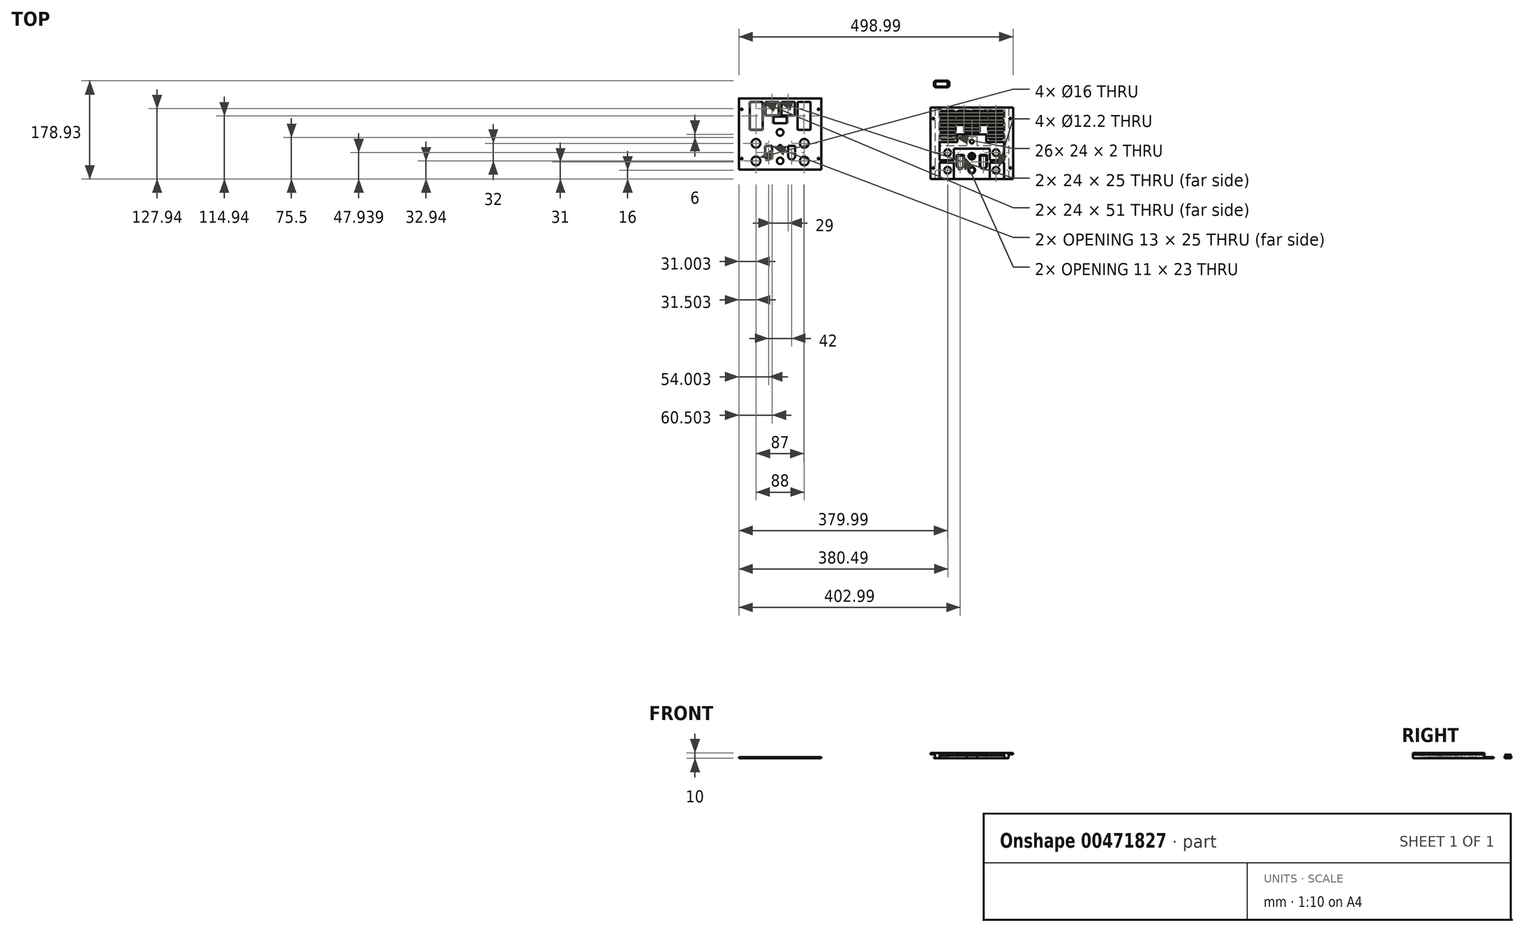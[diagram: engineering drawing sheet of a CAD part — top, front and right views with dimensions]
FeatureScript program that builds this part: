
annotation { "Feature Type Name" : "Feature", "Feature Type Description" : "" }
export const myFeature = defineFeature(function(context is Context, id is Id, definition is map)
    precondition{}
    {
        {
            var Q0;
            Q0=qCreatedBy(makeId("Top.planeOp"),FACE);
            var sketch = newSketch(context, id + "F0", { "sketchPlane" : qUnion([Q0])});
            skLineSegment(sketch, "E0.bottom", {"start": v(75, -65) * mm, "end": v(-75, -65) * mm});
            skLineSegment(sketch, "E0.top", {"start": v(75, 65) * mm, "end": v(-75, 65) * mm});
            skLineSegment(sketch, "E0.left", {"start": v(75, -65) * mm, "end": v(75, 65) * mm});
            skLineSegment(sketch, "E0.right", {"start": v(-75, -65) * mm, "end": v(-75, 65) * mm});
            skPoint(sketch, "E0.middle", {"position": v(0, 0) * mm});
            skLineSegment(sketch, "E1.bottom", {"start": v(-75, 65) * mm, "end": v(-65, 65) * mm, "construction": true});
            skLineSegment(sketch, "E1.top", {"start": v(-75, -65) * mm, "end": v(-65, -65) * mm, "construction": true});
            skLineSegment(sketch, "E1.left", {"start": v(-75, 65) * mm, "end": v(-75, -65) * mm, "construction": true});
            skLineSegment(sketch, "E1.right", {"start": v(-65, 65) * mm, "end": v(-65, -65) * mm, "construction": true});
            skLineSegment(sketch, "E2.bottom", {"start": v(75, -65) * mm, "end": v(65, -65) * mm, "construction": true});
            skLineSegment(sketch, "E2.top", {"start": v(75, 65) * mm, "end": v(65, 65) * mm, "construction": true});
            skLineSegment(sketch, "E2.left", {"start": v(75, -65) * mm, "end": v(75, 65) * mm, "construction": true});
            skLineSegment(sketch, "E2.right", {"start": v(65, -65) * mm, "end": v(65, 65) * mm, "construction": true});
            skCircle(sketch, "E3", {"center": v(-44, -17) * mm, "radius": 6.1 * mm});
            skCircle(sketch, "E4", {"center": v(-44, -49) * mm, "radius": 6.1 * mm});
            skCircle(sketch, "E5", {"center": v(44, -17) * mm, "radius": 6.1 * mm});
            skCircle(sketch, "E6", {"center": v(44, -49) * mm, "radius": 6.1 * mm});
            skCircle(sketch, "E7", {"center": v(0, -49) * mm, "radius": 6 * mm});
            skCircle(sketch, "E8", {"center": v(0, -23.67) * mm, "radius": 6 * mm});
            skLineSegment(sketch, "E9.bottom", {"start": v(-27.5, -21.5) * mm, "end": v(-14.5, -21.5) * mm});
            skLineSegment(sketch, "E9.top", {"start": v(-21, -46.5) * mm, "end": v(-21, -46.5) * mm});
            skLineSegment(sketch, "E9.left", {"start": v(-27.5, -21.5) * mm, "end": v(-27.5, -40) * mm});
            skLineSegment(sketch, "E9.right", {"start": v(-14.5, -21.5) * mm, "end": v(-14.5, -40) * mm});
            skPoint(sketch, "E10.visualSharp", {"position": v(-27.5, -46.5) * mm});
            skArc(sketch, "E10.filletArc", {"start": v(-27.5, -40) * mm, "mid": v(-25.6, -44.6) * mm, "end": v(-21, -46.5) * mm});
            skPoint(sketch, "E11.visualSharp", {"position": v(-14.5, -46.5) * mm});
            skArc(sketch, "E11.filletArc", {"start": v(-21, -46.5) * mm, "mid": v(-16.4, -44.6) * mm, "end": v(-14.5, -40) * mm});
            skLineSegment(sketch, "E12.bottom", {"start": v(14.5, -21.5) * mm, "end": v(27.5, -21.5) * mm});
            skLineSegment(sketch, "E12.top", {"start": v(21, -46.5) * mm, "end": v(21, -46.5) * mm});
            skLineSegment(sketch, "E12.left", {"start": v(14.5, -21.5) * mm, "end": v(14.5, -40) * mm});
            skLineSegment(sketch, "E12.right", {"start": v(27.5, -21.5) * mm, "end": v(27.5, -40) * mm});
            skPoint(sketch, "E13.visualSharp", {"position": v(14.5, -46.5) * mm});
            skArc(sketch, "E13.filletArc", {"start": v(14.5, -40) * mm, "mid": v(16.4, -44.6) * mm, "end": v(21, -46.5) * mm});
            skPoint(sketch, "E14.visualSharp", {"position": v(27.5, -46.5) * mm});
            skArc(sketch, "E14.filletArc", {"start": v(21, -46.5) * mm, "mid": v(25.6, -44.6) * mm, "end": v(27.5, -40) * mm});
            skLineSegment(sketch, "E15.bottom", {"start": v(56.5, 6.5) * mm, "end": v(-56.5, 6.5) * mm});
            skLineSegment(sketch, "E15.top", {"start": v(56.5, 59.5) * mm, "end": v(-56.5, 59.5) * mm, "construction": true});
            skLineSegment(sketch, "E15.left", {"start": v(56.5, 6.5) * mm, "end": v(56.5, 59.5) * mm, "construction": true});
            skLineSegment(sketch, "E15.right", {"start": v(-56.5, 6.5) * mm, "end": v(-56.5, 59.5) * mm, "construction": true});
            skPoint(sketch, "E15.middle", {"position": v(0, 33) * mm});
            skCircle(sketch, "E16", {"center": v(-44, -17) * mm, "radius": 8 * mm, "construction": true});
            skCircle(sketch, "E17", {"center": v(-44, -49) * mm, "radius": 8 * mm, "construction": true});
            skCircle(sketch, "E18", {"center": v(44, -49) * mm, "radius": 8 * mm, "construction": true});
            skCircle(sketch, "E19", {"center": v(44, -17) * mm, "radius": 8 * mm, "construction": true});
            skLineSegment(sketch, "E20.bottom", {"start": v(-31.5, 46.5) * mm, "end": v(-55.5, 46.5) * mm, "construction": true});
            skLineSegment(sketch, "E20.top", {"start": v(-31.5, 58.5) * mm, "end": v(-55.5, 58.5) * mm, "construction": true});
            skLineSegment(sketch, "E20.left", {"start": v(-31.5, 46.5) * mm, "end": v(-31.5, 58.5) * mm, "construction": true});
            skLineSegment(sketch, "E20.right", {"start": v(-55.5, 46.5) * mm, "end": v(-55.5, 58.5) * mm, "construction": true});
            skPoint(sketch, "E20.middle", {"position": v(-43.5, 52.5) * mm});
            skLineSegment(sketch, "E21.bottom", {"start": v(-31.5, 45.5) * mm, "end": v(-55.5, 45.5) * mm, "construction": true});
            skLineSegment(sketch, "E21.top", {"start": v(-31.5, 33.5) * mm, "end": v(-55.5, 33.5) * mm, "construction": true});
            skLineSegment(sketch, "E21.left", {"start": v(-31.5, 45.5) * mm, "end": v(-31.5, 33.5) * mm, "construction": true});
            skLineSegment(sketch, "E21.right", {"start": v(-55.5, 45.5) * mm, "end": v(-55.5, 33.5) * mm, "construction": true});
            skPoint(sketch, "E21.middle", {"position": v(-43.5, 39.5) * mm});
            skLineSegment(sketch, "E22.bottom", {"start": v(-31.5, 32.5) * mm, "end": v(-55.5, 32.5) * mm, "construction": true});
            skLineSegment(sketch, "E22.top", {"start": v(-31.5, 20.5) * mm, "end": v(-55.5, 20.5) * mm, "construction": true});
            skLineSegment(sketch, "E22.left", {"start": v(-31.5, 32.5) * mm, "end": v(-31.5, 20.5) * mm, "construction": true});
            skLineSegment(sketch, "E22.right", {"start": v(-55.5, 32.5) * mm, "end": v(-55.5, 20.5) * mm, "construction": true});
            skPoint(sketch, "E22.middle", {"position": v(-43.5, 26.5) * mm});
            skLineSegment(sketch, "E23.bottom", {"start": v(-31.5, 19.5) * mm, "end": v(-55.5, 19.5) * mm, "construction": true});
            skLineSegment(sketch, "E23.top", {"start": v(-31.5, 7.5) * mm, "end": v(-55.5, 7.5) * mm, "construction": true});
            skLineSegment(sketch, "E23.left", {"start": v(-31.5, 19.5) * mm, "end": v(-31.5, 7.5) * mm, "construction": true});
            skLineSegment(sketch, "E23.right", {"start": v(-55.5, 19.5) * mm, "end": v(-55.5, 7.5) * mm, "construction": true});
            skPoint(sketch, "E23.middle", {"position": v(-43.5, 13.5) * mm});
            skLineSegment(sketch, "E24.bottom", {"start": v(55.5, 32.5) * mm, "end": v(31.5, 32.5) * mm, "construction": true});
            skLineSegment(sketch, "E24.top", {"start": v(55.5, 20.5) * mm, "end": v(31.5, 20.5) * mm, "construction": true});
            skLineSegment(sketch, "E24.left", {"start": v(55.5, 32.5) * mm, "end": v(55.5, 20.5) * mm, "construction": true});
            skLineSegment(sketch, "E24.right", {"start": v(31.5, 32.5) * mm, "end": v(31.5, 20.5) * mm, "construction": true});
            skPoint(sketch, "E24.middle", {"position": v(43.5, 26.5) * mm});
            skLineSegment(sketch, "E25.bottom", {"start": v(55.5, 19.5) * mm, "end": v(31.5, 19.5) * mm, "construction": true});
            skLineSegment(sketch, "E25.top", {"start": v(55.5, 7.5) * mm, "end": v(31.5, 7.5) * mm, "construction": true});
            skLineSegment(sketch, "E25.left", {"start": v(55.5, 19.5) * mm, "end": v(55.5, 7.5) * mm, "construction": true});
            skLineSegment(sketch, "E25.right", {"start": v(31.5, 19.5) * mm, "end": v(31.5, 7.5) * mm, "construction": true});
            skPoint(sketch, "E25.middle", {"position": v(43.5, 13.5) * mm});
            skPoint(sketch, "E25.middle.positionSnap0", {"position": v(43.5, 20.5) * mm});
            skPoint(sketch, "E25.centerSnap0", {"position": v(43.5, 20.5) * mm});
            skLineSegment(sketch, "E26.bottom", {"start": v(12, 20.33) * mm, "end": v(-12, 20.33) * mm, "construction": true});
            skLineSegment(sketch, "E26.top", {"start": v(12, 32.33) * mm, "end": v(-12, 32.33) * mm, "construction": true});
            skLineSegment(sketch, "E26.left", {"start": v(12, 20.33) * mm, "end": v(12, 32.33) * mm, "construction": true});
            skLineSegment(sketch, "E26.right", {"start": v(-12, 20.33) * mm, "end": v(-12, 32.33) * mm, "construction": true});
            skPoint(sketch, "E26.middle", {"position": v(0, 26.33) * mm});
            skCircle(sketch, "E27", {"center": v(-70, 45) * mm, "radius": 1.5 * mm});
            skCircle(sketch, "E28", {"center": v(-70, -45) * mm, "radius": 1.5 * mm});
            skCircle(sketch, "E29", {"center": v(70, 45) * mm, "radius": 1.5 * mm});
            skCircle(sketch, "E30", {"center": v(70, -45) * mm, "radius": 1.5 * mm});
            skCircle(sketch, "E31", {"center": v(0, 3) * mm, "radius": 3.5 * mm});
            skCircle(sketch, "E32", {"center": v(0, 3) * mm, "radius": 6.15 * mm, "construction": true});
            skLineSegment(sketch, "E33.bottom", {"start": v(-30.46, 6.5) * mm, "end": v(-12.96, 6.5) * mm});
            skLineSegment(sketch, "E33.top", {"start": v(-30.46, 32.33) * mm, "end": v(-12.96, 32.33) * mm, "construction": true});
            skLineSegment(sketch, "E33.left", {"start": v(-30.46, 6.5) * mm, "end": v(-30.46, 32.33) * mm, "construction": true});
            skLineSegment(sketch, "E33.right", {"start": v(-12.96, 19.33) * mm, "end": v(-12.96, 32.33) * mm, "construction": true});
            skLineSegment(sketch, "E34.bottom", {"start": v(13.04, 32.33) * mm, "end": v(30.54, 32.33) * mm, "construction": true});
            skLineSegment(sketch, "E34.top", {"start": v(13.04, 6.5) * mm, "end": v(30.54, 6.5) * mm});
            skLineSegment(sketch, "E34.left", {"start": v(13.04, 32.33) * mm, "end": v(13.04, 19.33) * mm, "construction": true});
            skLineSegment(sketch, "E34.right", {"start": v(30.54, 32.33) * mm, "end": v(30.54, 6.5) * mm, "construction": true});
            skLineSegment(sketch, "E35", {"start": v(-12.96, 19.33) * mm, "end": v(13.04, 19.33) * mm, "construction": true});
            skLineSegment(sketch, "E36.bottom", {"start": v(-55.5, 57.5) * mm, "end": v(-57.5, 57.5) * mm, "construction": true});
            skLineSegment(sketch, "E36.top", {"start": v(-55.5, 47.5) * mm, "end": v(-57.5, 47.5) * mm, "construction": true});
            skLineSegment(sketch, "E36.left", {"start": v(-55.5, 57.5) * mm, "end": v(-55.5, 47.5) * mm, "construction": true});
            skLineSegment(sketch, "E36.right", {"start": v(-57.5, 57.5) * mm, "end": v(-57.5, 47.5) * mm, "construction": true});
            skLineSegment(sketch, "E37.bottom", {"start": v(-31.5, 57.5) * mm, "end": v(-29.5, 57.5) * mm, "construction": true});
            skLineSegment(sketch, "E37.top", {"start": v(-31.5, 47.5) * mm, "end": v(-29.5, 47.5) * mm, "construction": true});
            skLineSegment(sketch, "E37.left", {"start": v(-31.5, 57.5) * mm, "end": v(-31.5, 47.5) * mm, "construction": true});
            skLineSegment(sketch, "E37.right", {"start": v(-29.5, 57.5) * mm, "end": v(-29.5, 47.5) * mm, "construction": true});
            skLineSegment(sketch, "E38.bottom", {"start": v(-55.5, 44.5) * mm, "end": v(-57.5, 44.5) * mm, "construction": true});
            skLineSegment(sketch, "E38.top", {"start": v(-55.5, 34.5) * mm, "end": v(-57.5, 34.5) * mm, "construction": true});
            skLineSegment(sketch, "E38.left", {"start": v(-55.5, 44.5) * mm, "end": v(-55.5, 34.5) * mm, "construction": true});
            skLineSegment(sketch, "E38.right", {"start": v(-57.5, 44.5) * mm, "end": v(-57.5, 34.5) * mm, "construction": true});
            skLineSegment(sketch, "E39.bottom", {"start": v(-31.5, 44.5) * mm, "end": v(-29.5, 44.5) * mm, "construction": true});
            skLineSegment(sketch, "E39.top", {"start": v(-31.5, 34.5) * mm, "end": v(-29.5, 34.5) * mm, "construction": true});
            skLineSegment(sketch, "E39.left", {"start": v(-31.5, 44.5) * mm, "end": v(-31.5, 34.5) * mm, "construction": true});
            skLineSegment(sketch, "E39.right", {"start": v(-29.5, 44.5) * mm, "end": v(-29.5, 34.5) * mm, "construction": true});
            skPoint(sketch, "E40.1.0.0", {"position": v(-14.5, 39.5) * mm});
            skLineSegment(sketch, "E40.1.0.1", {"start": v(-2.5, 44.5) * mm, "end": v(-2.5, 34.5) * mm, "construction": true});
            skLineSegment(sketch, "E40.1.0.2", {"start": v(-2.5, 45.5) * mm, "end": v(-26.5, 45.5) * mm, "construction": true});
            skLineSegment(sketch, "E40.1.0.3", {"start": v(-26.5, 44.5) * mm, "end": v(-26.5, 34.5) * mm, "construction": true});
            skLineSegment(sketch, "E40.1.0.4", {"start": v(-2.5, 58.5) * mm, "end": v(-26.5, 58.5) * mm, "construction": true});
            skLineSegment(sketch, "E40.1.0.5", {"start": v(-0.5, 44.5) * mm, "end": v(-0.5, 34.5) * mm, "construction": true});
            skLineSegment(sketch, "E40.1.0.6", {"start": v(-2.5, 47.5) * mm, "end": v(-0.5, 47.5) * mm, "construction": true});
            skLineSegment(sketch, "E40.1.0.7", {"start": v(-26.5, 57.5) * mm, "end": v(-26.5, 47.5) * mm, "construction": true});
            skLineSegment(sketch, "E40.1.0.8", {"start": v(-2.5, 46.5) * mm, "end": v(-26.5, 46.5) * mm, "construction": true});
            skLineSegment(sketch, "E40.1.0.9", {"start": v(-2.5, 33.5) * mm, "end": v(-26.5, 33.5) * mm, "construction": true});
            skLineSegment(sketch, "E40.1.0.10", {"start": v(-28.5, 44.5) * mm, "end": v(-28.5, 34.5) * mm, "construction": true});
            skLineSegment(sketch, "E40.1.0.11", {"start": v(-26.5, 47.5) * mm, "end": v(-28.5, 47.5) * mm, "construction": true});
            skLineSegment(sketch, "E40.1.0.12", {"start": v(-28.5, 57.5) * mm, "end": v(-28.5, 47.5) * mm, "construction": true});
            skLineSegment(sketch, "E40.1.0.13", {"start": v(-26.5, 34.5) * mm, "end": v(-28.5, 34.5) * mm, "construction": true});
            skLineSegment(sketch, "E40.1.0.14", {"start": v(-0.5, 57.5) * mm, "end": v(-0.5, 47.5) * mm, "construction": true});
            skLineSegment(sketch, "E40.1.0.15", {"start": v(-2.5, 46.5) * mm, "end": v(-2.5, 58.5) * mm, "construction": true});
            skLineSegment(sketch, "E40.1.0.16", {"start": v(-2.5, 44.5) * mm, "end": v(-0.5, 44.5) * mm, "construction": true});
            skLineSegment(sketch, "E40.1.0.17", {"start": v(-2.5, 57.5) * mm, "end": v(-0.5, 57.5) * mm, "construction": true});
            skLineSegment(sketch, "E40.1.0.18", {"start": v(-2.5, 34.5) * mm, "end": v(-0.5, 34.5) * mm, "construction": true});
            skLineSegment(sketch, "E40.1.0.19", {"start": v(-26.5, 57.5) * mm, "end": v(-28.5, 57.5) * mm, "construction": true});
            skPoint(sketch, "E40.1.0.20", {"position": v(-14.5, 52.5) * mm});
            skLineSegment(sketch, "E40.1.0.21", {"start": v(-26.5, 44.5) * mm, "end": v(-28.5, 44.5) * mm, "construction": true});
            skLineSegment(sketch, "E40.1.0.22", {"start": v(-2.5, 57.5) * mm, "end": v(-2.5, 47.5) * mm, "construction": true});
            skLineSegment(sketch, "E40.1.0.23", {"start": v(-26.5, 46.5) * mm, "end": v(-26.5, 58.5) * mm, "construction": true});
            skLineSegment(sketch, "E40.1.0.24", {"start": v(-26.5, 45.5) * mm, "end": v(-26.5, 33.5) * mm, "construction": true});
            skLineSegment(sketch, "E40.1.0.25", {"start": v(-2.5, 45.5) * mm, "end": v(-2.5, 33.5) * mm, "construction": true});
            skPoint(sketch, "E40.2.0.0", {"position": v(14.5, 39.5) * mm});
            skLineSegment(sketch, "E40.2.0.1", {"start": v(26.5, 44.5) * mm, "end": v(26.5, 34.5) * mm, "construction": true});
            skLineSegment(sketch, "E40.2.0.2", {"start": v(26.5, 45.5) * mm, "end": v(2.5, 45.5) * mm, "construction": true});
            skLineSegment(sketch, "E40.2.0.3", {"start": v(2.5, 44.5) * mm, "end": v(2.5, 34.5) * mm, "construction": true});
            skLineSegment(sketch, "E40.2.0.4", {"start": v(26.5, 58.5) * mm, "end": v(2.5, 58.5) * mm, "construction": true});
            skLineSegment(sketch, "E40.2.0.5", {"start": v(28.5, 44.5) * mm, "end": v(28.5, 34.5) * mm, "construction": true});
            skLineSegment(sketch, "E40.2.0.6", {"start": v(26.5, 47.5) * mm, "end": v(28.5, 47.5) * mm, "construction": true});
            skLineSegment(sketch, "E40.2.0.7", {"start": v(2.5, 57.5) * mm, "end": v(2.5, 47.5) * mm, "construction": true});
            skLineSegment(sketch, "E40.2.0.8", {"start": v(26.5, 46.5) * mm, "end": v(2.5, 46.5) * mm, "construction": true});
            skLineSegment(sketch, "E40.2.0.9", {"start": v(26.5, 33.5) * mm, "end": v(2.5, 33.5) * mm, "construction": true});
            skLineSegment(sketch, "E40.2.0.10", {"start": v(0.5, 44.5) * mm, "end": v(0.5, 34.5) * mm, "construction": true});
            skLineSegment(sketch, "E40.2.0.11", {"start": v(2.5, 47.5) * mm, "end": v(0.5, 47.5) * mm, "construction": true});
            skLineSegment(sketch, "E40.2.0.12", {"start": v(0.5, 57.5) * mm, "end": v(0.5, 47.5) * mm, "construction": true});
            skLineSegment(sketch, "E40.2.0.13", {"start": v(2.5, 34.5) * mm, "end": v(0.5, 34.5) * mm, "construction": true});
            skLineSegment(sketch, "E40.2.0.14", {"start": v(28.5, 57.5) * mm, "end": v(28.5, 47.5) * mm, "construction": true});
            skLineSegment(sketch, "E40.2.0.15", {"start": v(26.5, 46.5) * mm, "end": v(26.5, 58.5) * mm, "construction": true});
            skLineSegment(sketch, "E40.2.0.16", {"start": v(26.5, 44.5) * mm, "end": v(28.5, 44.5) * mm, "construction": true});
            skLineSegment(sketch, "E40.2.0.17", {"start": v(26.5, 57.5) * mm, "end": v(28.5, 57.5) * mm, "construction": true});
            skLineSegment(sketch, "E40.2.0.18", {"start": v(26.5, 34.5) * mm, "end": v(28.5, 34.5) * mm, "construction": true});
            skLineSegment(sketch, "E40.2.0.19", {"start": v(2.5, 57.5) * mm, "end": v(0.5, 57.5) * mm, "construction": true});
            skPoint(sketch, "E40.2.0.20", {"position": v(14.5, 52.5) * mm});
            skLineSegment(sketch, "E40.2.0.21", {"start": v(2.5, 44.5) * mm, "end": v(0.5, 44.5) * mm, "construction": true});
            skLineSegment(sketch, "E40.2.0.22", {"start": v(26.5, 57.5) * mm, "end": v(26.5, 47.5) * mm, "construction": true});
            skLineSegment(sketch, "E40.2.0.23", {"start": v(2.5, 46.5) * mm, "end": v(2.5, 58.5) * mm, "construction": true});
            skLineSegment(sketch, "E40.2.0.24", {"start": v(2.5, 45.5) * mm, "end": v(2.5, 33.5) * mm, "construction": true});
            skLineSegment(sketch, "E40.2.0.25", {"start": v(26.5, 45.5) * mm, "end": v(26.5, 33.5) * mm, "construction": true});
            skPoint(sketch, "E40.3.0.0", {"position": v(43.5, 39.5) * mm});
            skLineSegment(sketch, "E40.3.0.1", {"start": v(55.5, 44.5) * mm, "end": v(55.5, 34.5) * mm, "construction": true});
            skLineSegment(sketch, "E40.3.0.2", {"start": v(55.5, 45.5) * mm, "end": v(31.5, 45.5) * mm, "construction": true});
            skLineSegment(sketch, "E40.3.0.3", {"start": v(31.5, 44.5) * mm, "end": v(31.5, 34.5) * mm, "construction": true});
            skLineSegment(sketch, "E40.3.0.4", {"start": v(55.5, 58.5) * mm, "end": v(31.5, 58.5) * mm, "construction": true});
            skLineSegment(sketch, "E40.3.0.5", {"start": v(57.5, 44.5) * mm, "end": v(57.5, 34.5) * mm, "construction": true});
            skLineSegment(sketch, "E40.3.0.6", {"start": v(55.5, 47.5) * mm, "end": v(57.5, 47.5) * mm, "construction": true});
            skLineSegment(sketch, "E40.3.0.7", {"start": v(31.5, 57.5) * mm, "end": v(31.5, 47.5) * mm, "construction": true});
            skLineSegment(sketch, "E40.3.0.8", {"start": v(55.5, 46.5) * mm, "end": v(31.5, 46.5) * mm, "construction": true});
            skLineSegment(sketch, "E40.3.0.9", {"start": v(55.5, 33.5) * mm, "end": v(31.5, 33.5) * mm, "construction": true});
            skLineSegment(sketch, "E40.3.0.10", {"start": v(29.5, 44.5) * mm, "end": v(29.5, 34.5) * mm, "construction": true});
            skLineSegment(sketch, "E40.3.0.11", {"start": v(31.5, 47.5) * mm, "end": v(29.5, 47.5) * mm, "construction": true});
            skLineSegment(sketch, "E40.3.0.12", {"start": v(29.5, 57.5) * mm, "end": v(29.5, 47.5) * mm, "construction": true});
            skLineSegment(sketch, "E40.3.0.13", {"start": v(31.5, 34.5) * mm, "end": v(29.5, 34.5) * mm, "construction": true});
            skLineSegment(sketch, "E40.3.0.14", {"start": v(57.5, 57.5) * mm, "end": v(57.5, 47.5) * mm, "construction": true});
            skLineSegment(sketch, "E40.3.0.15", {"start": v(55.5, 46.5) * mm, "end": v(55.5, 58.5) * mm, "construction": true});
            skLineSegment(sketch, "E40.3.0.16", {"start": v(55.5, 44.5) * mm, "end": v(57.5, 44.5) * mm, "construction": true});
            skLineSegment(sketch, "E40.3.0.17", {"start": v(55.5, 57.5) * mm, "end": v(57.5, 57.5) * mm, "construction": true});
            skLineSegment(sketch, "E40.3.0.18", {"start": v(55.5, 34.5) * mm, "end": v(57.5, 34.5) * mm, "construction": true});
            skLineSegment(sketch, "E40.3.0.19", {"start": v(31.5, 57.5) * mm, "end": v(29.5, 57.5) * mm, "construction": true});
            skPoint(sketch, "E40.3.0.20", {"position": v(43.5, 52.5) * mm});
            skLineSegment(sketch, "E40.3.0.21", {"start": v(31.5, 44.5) * mm, "end": v(29.5, 44.5) * mm, "construction": true});
            skLineSegment(sketch, "E40.3.0.22", {"start": v(55.5, 57.5) * mm, "end": v(55.5, 47.5) * mm, "construction": true});
            skLineSegment(sketch, "E40.3.0.23", {"start": v(31.5, 46.5) * mm, "end": v(31.5, 58.5) * mm, "construction": true});
            skLineSegment(sketch, "E40.3.0.24", {"start": v(31.5, 45.5) * mm, "end": v(31.5, 33.5) * mm, "construction": true});
            skLineSegment(sketch, "E40.3.0.25", {"start": v(55.5, 45.5) * mm, "end": v(55.5, 33.5) * mm, "construction": true});
            skLineSegment(sketch, "E40.direction1", {"start": v(-57.5, 34.5) * mm, "end": v(-28.5, 34.5) * mm, "construction": true});
            skSolve(sketch);
        }
        {
            var Q0;
            Q0=makeQuery(id+"F0.imprint","IMPRINT",FACE,{"disambiguationData":[TD([[makeQuery(id+"F0.imprint","IMPRINT",EDGE,{"derivedFrom":sQuery(id+"F0.wireOp",EDGE,"E0.bottom")}),-1.0]])]});
            var Q1;
            {var subQ3=sQuery(id+"F0.wireOp",EDGE,"E33.bottom");Q1=makeQuery(id+"F0.imprint","IMPRINT",FACE,{"disambiguationData":[TD([[makeQuery(id+"F0.imprint","IMPRINT",EDGE,{"derivedFrom":subQ3}),1.0]])]});}
            extrude(context, id + "F1", {"entities" : qUnion([Q0, Q1]), "depth" : 10 * mm});
        }
        {
            var Q0;
            Q0=qCreatedBy(makeId("Top.planeOp"),FACE);
            var sketch = newSketch(context, id + "F2", { "sketchPlane" : qUnion([Q0])});
            skLineSegment(sketch, "E41.bottom", {"start": v(-273.99, -48.06) * mm, "end": v(-423.99, -48.06) * mm});
            skLineSegment(sketch, "E41.top", {"start": v(-273.99, 81.94) * mm, "end": v(-423.99, 81.94) * mm});
            skLineSegment(sketch, "E41.left", {"start": v(-273.99, -48.06) * mm, "end": v(-273.99, 81.94) * mm});
            skLineSegment(sketch, "E41.right", {"start": v(-423.99, -48.06) * mm, "end": v(-423.99, 81.94) * mm});
            skPoint(sketch, "E41.middle", {"position": v(-348.99, 16.94) * mm});
            skLineSegment(sketch, "E42.bottom", {"start": v(-423.99, 81.94) * mm, "end": v(-413.99, 81.94) * mm, "construction": true});
            skLineSegment(sketch, "E42.top", {"start": v(-423.99, -48.06) * mm, "end": v(-413.99, -48.06) * mm, "construction": true});
            skLineSegment(sketch, "E42.left", {"start": v(-423.99, 81.94) * mm, "end": v(-423.99, -48.06) * mm, "construction": true});
            skLineSegment(sketch, "E42.right", {"start": v(-413.99, 81.94) * mm, "end": v(-413.99, -48.06) * mm, "construction": true});
            skLineSegment(sketch, "E43.bottom", {"start": v(-273.99, -48.06) * mm, "end": v(-283.99, -48.06) * mm, "construction": true});
            skLineSegment(sketch, "E43.top", {"start": v(-273.99, 81.94) * mm, "end": v(-283.99, 81.94) * mm, "construction": true});
            skLineSegment(sketch, "E43.left", {"start": v(-273.99, -48.06) * mm, "end": v(-273.99, 81.94) * mm, "construction": true});
            skLineSegment(sketch, "E43.right", {"start": v(-283.99, -48.06) * mm, "end": v(-283.99, 81.94) * mm, "construction": true});
            skCircle(sketch, "E44", {"center": v(-392.99, -0.06) * mm, "radius": 6.1 * mm, "construction": true});
            skCircle(sketch, "E45", {"center": v(-392.99, -32.06) * mm, "radius": 6.1 * mm, "construction": true});
            skCircle(sketch, "E46", {"center": v(-304.99, -0.06) * mm, "radius": 6.1 * mm, "construction": true});
            skCircle(sketch, "E47", {"center": v(-304.99, -32.06) * mm, "radius": 6.1 * mm, "construction": true});
            skCircle(sketch, "E48", {"center": v(-348.99, -32.06) * mm, "radius": 6 * mm});
            skCircle(sketch, "E49", {"center": v(-348.99, -6.73) * mm, "radius": 3.5 * mm});
            skLineSegment(sketch, "E50.bottom", {"start": v(-376.49, -4.56) * mm, "end": v(-363.49, -4.56) * mm});
            skLineSegment(sketch, "E50.top", {"start": v(-369.99, -29.56) * mm, "end": v(-369.99, -29.56) * mm});
            skLineSegment(sketch, "E50.left", {"start": v(-376.49, -4.56) * mm, "end": v(-376.49, -23.06) * mm});
            skLineSegment(sketch, "E50.right", {"start": v(-363.49, -4.56) * mm, "end": v(-363.49, -23.06) * mm});
            skPoint(sketch, "E51.visualSharp", {"position": v(-376.49, -29.56) * mm});
            skArc(sketch, "E51.filletArc", {"start": v(-376.49, -23.06) * mm, "mid": v(-374.58, -27.66) * mm, "end": v(-369.99, -29.56) * mm});
            skPoint(sketch, "E52.visualSharp", {"position": v(-363.49, -29.56) * mm});
            skArc(sketch, "E52.filletArc", {"start": v(-369.99, -29.56) * mm, "mid": v(-365.4, -27.66) * mm, "end": v(-363.49, -23.06) * mm});
            skLineSegment(sketch, "E53.bottom", {"start": v(-334.49, -4.56) * mm, "end": v(-321.49, -4.56) * mm});
            skLineSegment(sketch, "E53.top", {"start": v(-327.99, -29.56) * mm, "end": v(-327.99, -29.56) * mm});
            skLineSegment(sketch, "E53.left", {"start": v(-334.49, -4.56) * mm, "end": v(-334.49, -23.06) * mm});
            skLineSegment(sketch, "E53.right", {"start": v(-321.49, -4.56) * mm, "end": v(-321.49, -23.06) * mm});
            skPoint(sketch, "E54.visualSharp", {"position": v(-334.49, -29.56) * mm});
            skArc(sketch, "E54.filletArc", {"start": v(-334.49, -23.06) * mm, "mid": v(-332.58, -27.66) * mm, "end": v(-327.99, -29.56) * mm});
            skPoint(sketch, "E55.visualSharp", {"position": v(-321.49, -29.56) * mm});
            skArc(sketch, "E55.filletArc", {"start": v(-327.99, -29.56) * mm, "mid": v(-323.4, -27.66) * mm, "end": v(-321.49, -23.06) * mm});
            skPoint(sketch, "E56.middle", {"position": v(-348.99, 49.94) * mm});
            skCircle(sketch, "E57", {"center": v(-392.99, -0.06) * mm, "radius": 8 * mm});
            skCircle(sketch, "E58", {"center": v(-392.99, -32.06) * mm, "radius": 8 * mm});
            skCircle(sketch, "E59", {"center": v(-304.99, -32.06) * mm, "radius": 8 * mm});
            skCircle(sketch, "E60", {"center": v(-304.99, -0.06) * mm, "radius": 8 * mm});
            skLineSegment(sketch, "E61.bottom", {"start": v(-380.49, 63.44) * mm, "end": v(-404.49, 63.44) * mm, "construction": true});
            skLineSegment(sketch, "E61.top", {"start": v(-380.49, 75.44) * mm, "end": v(-404.49, 75.44) * mm, "construction": true});
            skLineSegment(sketch, "E61.left", {"start": v(-380.49, 63.44) * mm, "end": v(-380.49, 75.44) * mm, "construction": true});
            skLineSegment(sketch, "E61.right", {"start": v(-404.49, 63.44) * mm, "end": v(-404.49, 75.44) * mm, "construction": true});
            skPoint(sketch, "E61.middle", {"position": v(-392.49, 69.44) * mm});
            skLineSegment(sketch, "E62.bottom", {"start": v(-380.49, 62.44) * mm, "end": v(-404.49, 62.44) * mm, "construction": true});
            skLineSegment(sketch, "E62.top", {"start": v(-380.49, 50.44) * mm, "end": v(-404.49, 50.44) * mm, "construction": true});
            skLineSegment(sketch, "E62.left", {"start": v(-380.49, 62.44) * mm, "end": v(-380.49, 50.44) * mm, "construction": true});
            skLineSegment(sketch, "E62.right", {"start": v(-404.49, 62.44) * mm, "end": v(-404.49, 50.44) * mm, "construction": true});
            skPoint(sketch, "E62.middle", {"position": v(-392.49, 56.44) * mm});
            skLineSegment(sketch, "E63.bottom", {"start": v(-380.49, 49.44) * mm, "end": v(-404.49, 49.44) * mm, "construction": true});
            skLineSegment(sketch, "E63.top", {"start": v(-380.49, 37.44) * mm, "end": v(-404.49, 37.44) * mm, "construction": true});
            skLineSegment(sketch, "E63.left", {"start": v(-380.49, 49.44) * mm, "end": v(-380.49, 37.44) * mm, "construction": true});
            skLineSegment(sketch, "E63.right", {"start": v(-404.49, 49.44) * mm, "end": v(-404.49, 37.44) * mm, "construction": true});
            skPoint(sketch, "E63.middle", {"position": v(-392.49, 43.44) * mm});
            skLineSegment(sketch, "E64.bottom", {"start": v(-380.49, 36.44) * mm, "end": v(-404.49, 36.44) * mm, "construction": true});
            skLineSegment(sketch, "E64.top", {"start": v(-380.49, 24.44) * mm, "end": v(-404.49, 24.44) * mm, "construction": true});
            skLineSegment(sketch, "E64.left", {"start": v(-380.49, 36.44) * mm, "end": v(-380.49, 24.44) * mm, "construction": true});
            skLineSegment(sketch, "E64.right", {"start": v(-404.49, 36.44) * mm, "end": v(-404.49, 24.44) * mm, "construction": true});
            skPoint(sketch, "E64.middle", {"position": v(-392.49, 30.44) * mm});
            skPoint(sketch, "E65.1.0.0", {"position": v(-363.49, 56.44) * mm});
            skLineSegment(sketch, "E65.1.0.1", {"start": v(-351.49, 62.44) * mm, "end": v(-351.49, 50.44) * mm, "construction": true});
            skLineSegment(sketch, "E65.1.0.2", {"start": v(-351.49, 62.44) * mm, "end": v(-375.49, 62.44) * mm, "construction": true});
            skLineSegment(sketch, "E65.1.0.3", {"start": v(-375.49, 63.44) * mm, "end": v(-375.49, 75.44) * mm, "construction": true});
            skLineSegment(sketch, "E65.1.0.4", {"start": v(-351.49, 75.44) * mm, "end": v(-375.49, 75.44) * mm, "construction": true});
            skPoint(sketch, "E65.1.0.5", {"position": v(-363.49, 69.44) * mm});
            skLineSegment(sketch, "E65.1.0.6", {"start": v(-351.49, 50.44) * mm, "end": v(-375.49, 50.44) * mm, "construction": true});
            skLineSegment(sketch, "E65.1.0.7", {"start": v(-351.49, 63.44) * mm, "end": v(-351.49, 75.44) * mm, "construction": true});
            skLineSegment(sketch, "E65.1.0.8", {"start": v(-375.49, 62.44) * mm, "end": v(-375.49, 50.44) * mm, "construction": true});
            skLineSegment(sketch, "E65.1.0.9", {"start": v(-351.49, 63.44) * mm, "end": v(-375.49, 63.44) * mm, "construction": true});
            skPoint(sketch, "E65.2.0.0", {"position": v(-334.49, 56.44) * mm});
            skLineSegment(sketch, "E65.2.0.1", {"start": v(-322.49, 62.44) * mm, "end": v(-322.49, 50.44) * mm, "construction": true});
            skLineSegment(sketch, "E65.2.0.2", {"start": v(-322.49, 62.44) * mm, "end": v(-346.49, 62.44) * mm, "construction": true});
            skLineSegment(sketch, "E65.2.0.3", {"start": v(-346.49, 63.44) * mm, "end": v(-346.49, 75.44) * mm, "construction": true});
            skLineSegment(sketch, "E65.2.0.4", {"start": v(-322.49, 75.44) * mm, "end": v(-346.49, 75.44) * mm, "construction": true});
            skPoint(sketch, "E65.2.0.5", {"position": v(-334.49, 69.44) * mm});
            skLineSegment(sketch, "E65.2.0.6", {"start": v(-322.49, 50.44) * mm, "end": v(-346.49, 50.44) * mm, "construction": true});
            skLineSegment(sketch, "E65.2.0.7", {"start": v(-322.49, 63.44) * mm, "end": v(-322.49, 75.44) * mm, "construction": true});
            skLineSegment(sketch, "E65.2.0.8", {"start": v(-346.49, 62.44) * mm, "end": v(-346.49, 50.44) * mm, "construction": true});
            skLineSegment(sketch, "E65.2.0.9", {"start": v(-322.49, 63.44) * mm, "end": v(-346.49, 63.44) * mm, "construction": true});
            skPoint(sketch, "E65.3.0.0", {"position": v(-305.49, 56.44) * mm});
            skLineSegment(sketch, "E65.3.0.1", {"start": v(-293.49, 62.44) * mm, "end": v(-293.49, 50.44) * mm, "construction": true});
            skLineSegment(sketch, "E65.3.0.2", {"start": v(-293.49, 62.44) * mm, "end": v(-317.49, 62.44) * mm, "construction": true});
            skLineSegment(sketch, "E65.3.0.3", {"start": v(-317.49, 63.44) * mm, "end": v(-317.49, 75.44) * mm, "construction": true});
            skLineSegment(sketch, "E65.3.0.4", {"start": v(-293.49, 75.44) * mm, "end": v(-317.49, 75.44) * mm, "construction": true});
            skPoint(sketch, "E65.3.0.5", {"position": v(-305.49, 69.44) * mm});
            skLineSegment(sketch, "E65.3.0.6", {"start": v(-293.49, 50.44) * mm, "end": v(-317.49, 50.44) * mm, "construction": true});
            skLineSegment(sketch, "E65.3.0.7", {"start": v(-293.49, 63.44) * mm, "end": v(-293.49, 75.44) * mm, "construction": true});
            skLineSegment(sketch, "E65.3.0.8", {"start": v(-317.49, 62.44) * mm, "end": v(-317.49, 50.44) * mm, "construction": true});
            skLineSegment(sketch, "E65.3.0.9", {"start": v(-293.49, 63.44) * mm, "end": v(-317.49, 63.44) * mm, "construction": true});
            skLineSegment(sketch, "E65.direction1", {"start": v(-404.49, 50.44) * mm, "end": v(-375.49, 50.44) * mm, "construction": true});
            skLineSegment(sketch, "E66.bottom", {"start": v(-293.49, 49.44) * mm, "end": v(-317.49, 49.44) * mm, "construction": true});
            skLineSegment(sketch, "E66.top", {"start": v(-293.49, 37.44) * mm, "end": v(-317.49, 37.44) * mm, "construction": true});
            skLineSegment(sketch, "E66.left", {"start": v(-293.49, 49.44) * mm, "end": v(-293.49, 37.44) * mm, "construction": true});
            skLineSegment(sketch, "E66.right", {"start": v(-317.49, 49.44) * mm, "end": v(-317.49, 37.44) * mm, "construction": true});
            skPoint(sketch, "E66.middle", {"position": v(-305.49, 43.44) * mm});
            skLineSegment(sketch, "E67.bottom", {"start": v(-293.49, 36.44) * mm, "end": v(-317.49, 36.44) * mm, "construction": true});
            skLineSegment(sketch, "E67.top", {"start": v(-293.49, 24.44) * mm, "end": v(-317.49, 24.44) * mm, "construction": true});
            skLineSegment(sketch, "E67.left", {"start": v(-293.49, 36.44) * mm, "end": v(-293.49, 24.44) * mm, "construction": true});
            skLineSegment(sketch, "E67.right", {"start": v(-317.49, 36.44) * mm, "end": v(-317.49, 24.44) * mm, "construction": true});
            skPoint(sketch, "E67.middle", {"position": v(-305.49, 30.44) * mm});
            skPoint(sketch, "E67.middle.positionSnap0", {"position": v(-305.49, 37.44) * mm});
            skPoint(sketch, "E67.centerSnap0", {"position": v(-305.49, 37.44) * mm});
            skLineSegment(sketch, "E68.bottom", {"start": v(-336.99, 36.44) * mm, "end": v(-360.99, 36.44) * mm, "construction": true});
            skLineSegment(sketch, "E68.top", {"start": v(-336.99, 48.44) * mm, "end": v(-360.99, 48.44) * mm, "construction": true});
            skLineSegment(sketch, "E68.left", {"start": v(-336.99, 36.44) * mm, "end": v(-336.99, 48.44) * mm, "construction": true});
            skLineSegment(sketch, "E68.right", {"start": v(-360.99, 36.44) * mm, "end": v(-360.99, 48.44) * mm, "construction": true});
            skPoint(sketch, "E68.middle", {"position": v(-348.99, 42.44) * mm});
            skCircle(sketch, "E69", {"center": v(-418.99, 61.94) * mm, "radius": 1.5 * mm});
            skCircle(sketch, "E70", {"center": v(-418.99, -28.06) * mm, "radius": 1.5 * mm});
            skCircle(sketch, "E71", {"center": v(-278.99, 61.94) * mm, "radius": 1.5 * mm});
            skCircle(sketch, "E72", {"center": v(-278.99, -28.06) * mm, "radius": 1.5 * mm});
            skCircle(sketch, "E73", {"center": v(-348.99, 19.94) * mm, "radius": 3.5 * mm, "construction": true});
            skCircle(sketch, "E74", {"center": v(-348.99, 19.94) * mm, "radius": 6.15 * mm});
            skLineSegment(sketch, "E75", {"start": v(-404.49, 75.44) * mm, "end": v(-404.49, 24.44) * mm});
            skLineSegment(sketch, "E76", {"start": v(-404.49, 24.44) * mm, "end": v(-380.49, 24.44) * mm});
            skLineSegment(sketch, "E77", {"start": v(-380.49, 24.44) * mm, "end": v(-380.49, 50.44) * mm});
            skLineSegment(sketch, "E78", {"start": v(-380.49, 50.44) * mm, "end": v(-360.99, 50.44) * mm});
            skLineSegment(sketch, "E79", {"start": v(-360.99, 50.44) * mm, "end": v(-360.99, 36.44) * mm});
            skLineSegment(sketch, "E80", {"start": v(-360.99, 36.44) * mm, "end": v(-336.99, 36.44) * mm});
            skLineSegment(sketch, "E81", {"start": v(-336.99, 36.44) * mm, "end": v(-336.99, 50.44) * mm});
            skLineSegment(sketch, "E82", {"start": v(-336.99, 50.44) * mm, "end": v(-317.49, 50.44) * mm});
            skLineSegment(sketch, "E83", {"start": v(-317.49, 50.44) * mm, "end": v(-317.49, 24.44) * mm});
            skLineSegment(sketch, "E84", {"start": v(-317.49, 24.44) * mm, "end": v(-293.49, 24.44) * mm});
            skLineSegment(sketch, "E85", {"start": v(-293.49, 24.44) * mm, "end": v(-293.49, 75.44) * mm});
            skLineSegment(sketch, "E86", {"start": v(-293.49, 75.44) * mm, "end": v(-404.49, 75.44) * mm});
            skLineSegment(sketch, "E87", {"start": v(-380.49, 50.44) * mm, "end": v(-380.49, 75.44) * mm});
            skLineSegment(sketch, "E88", {"start": v(-375.49, 75.44) * mm, "end": v(-375.49, 50.44) * mm});
            skLineSegment(sketch, "E89", {"start": v(-322.49, 50.44) * mm, "end": v(-322.49, 75.44) * mm});
            skLineSegment(sketch, "E90", {"start": v(-317.49, 75.44) * mm, "end": v(-317.49, 50.44) * mm});
            skLineSegment(sketch, "E91", {"start": v(-360.99, 50.44) * mm, "end": v(-351.49, 50.44) * mm});
            skLineSegment(sketch, "E92", {"start": v(-351.49, 75.44) * mm, "end": v(-351.49, 50.44) * mm});
            skLineSegment(sketch, "E93", {"start": v(-346.49, 50.44) * mm, "end": v(-346.49, 75.44) * mm});
            skLineSegment(sketch, "E94", {"start": v(-336.99, 50.44) * mm, "end": v(-346.49, 50.44) * mm});
            skLineSegment(sketch, "E95", {"start": v(-360.99, 48.44) * mm, "end": v(-336.99, 48.44) * mm});
            skSolve(sketch);
        }
        {
            var Q0;
            Q0=makeQuery(id+"F2.imprint","IMPRINT",FACE,{"disambiguationData":[TD([[makeQuery(id+"F2.imprint","IMPRINT",EDGE,{"derivedFrom":sQuery(id+"F2.wireOp",EDGE,"E41.bottom")}),-1.0]])]});
            var Q1;
            {var subQ3=sQuery(id+"F2.wireOp",EDGE,"1b6c74bc-5b00-42bc-9f1d-b8e6521042cd.bottom");Q1=makeQuery(id+"F2.imprint","IMPRINT",FACE,{"disambiguationData":[TD([[makeQuery(id+"F2.imprint","IMPRINT",EDGE,{"derivedFrom":subQ3}),1.0]])]});}
            var Q2;
            {var subQ0=sQuery(id+"F2.wireOp",EDGE,"E87");Q2=makeQuery(id+"F2.imprint","IMPRINT",FACE,{"disambiguationData":[TD([[makeQuery(id+"F2.imprint","IMPRINT",EDGE,{"derivedFrom":subQ0}),-1.0]])]});}
            var Q3;
            {var subQ0=sQuery(id+"F2.wireOp",EDGE,"E91");Q3=makeQuery(id+"F2.imprint","IMPRINT",FACE,{"disambiguationData":[TD([[makeQuery(id+"F2.imprint","IMPRINT",EDGE,{"derivedFrom":subQ0}),-1.0]])]});}
            var Q4;
            {var subQ2=sQuery(id+"F2.wireOp",EDGE,"E89");Q4=makeQuery(id+"F2.imprint","IMPRINT",FACE,{"disambiguationData":[TD([[makeQuery(id+"F2.imprint","IMPRINT",EDGE,{"derivedFrom":subQ2}),-1.0]])]});}
            extrude(context, id + "F3", {"entities" : qUnion([Q0, Q1, Q2, Q3, Q4]), "depth" : 2 * mm});
        }
        {
            var Q0;
            Q0=makeQuery(id+"F1.opExtrude","SWEPT_FACE",FACE,{"disambiguationData":[OSD([sQuery(id+"F0.wireOp",EDGE,"E0.bottom")])]});
            var sketch = newSketch(context, id + "F4", { "sketchPlane" : qUnion([Q0])});
            skLineSegment(sketch, "E96.bottom", {"start": v(-75, 0) * mm, "end": v(-67, 0) * mm});
            skLineSegment(sketch, "E96.top", {"start": v(-75, 7) * mm, "end": v(-67, 7) * mm});
            skLineSegment(sketch, "E96.left", {"start": v(-75, 0) * mm, "end": v(-75, 7) * mm});
            skLineSegment(sketch, "E96.right", {"start": v(-67, 0) * mm, "end": v(-67, 7) * mm});
            skLineSegment(sketch, "E97.bottom", {"start": v(75, 0) * mm, "end": v(67, 0) * mm});
            skLineSegment(sketch, "E97.top", {"start": v(75, 7) * mm, "end": v(67, 7) * mm});
            skLineSegment(sketch, "E97.left", {"start": v(75, 0) * mm, "end": v(75, 7) * mm});
            skLineSegment(sketch, "E97.right", {"start": v(67, 0) * mm, "end": v(67, 7) * mm});
            skSolve(sketch);
        }
        {
            var Q0;
            Q0 = qSketchRegion(id + "F4", true);
            extrude(context, id + "F5", {"entities" : qUnion([Q0]), "operationType" : NewBodyOperationType.REMOVE, "oppositeDirection" : true, "depth" : 137.4 * mm});
        }
        {
            var Q0;
            Q0=makeQuery(id+"F1.opExtrude","CAP_FACE",FACE,{"disambiguationData":[OSD([sQuery(id+"F0.wireOp",EDGE,"E0.bottom"),sQuery(id+"F0.wireOp",EDGE,"E0.top"),sQuery(id+"F0.wireOp",EDGE,"E0.left"),sQuery(id+"F0.wireOp",EDGE,"E0.right"),sQuery(id+"F0.wireOp",EDGE,"E3"),sQuery(id+"F0.wireOp",EDGE,"E4"),sQuery(id+"F0.wireOp",EDGE,"E5"),sQuery(id+"F0.wireOp",EDGE,"E6"),sQuery(id+"F0.wireOp",EDGE,"E7"),sQuery(id+"F0.wireOp",EDGE,"E8"),sQuery(id+"F0.wireOp",EDGE,"E9.bottom"),sQuery(id+"F0.wireOp",EDGE,"E9.left"),sQuery(id+"F0.wireOp",EDGE,"E9.right"),sQuery(id+"F0.wireOp",EDGE,"E10.filletArc"),sQuery(id+"F0.wireOp",EDGE,"E11.filletArc"),sQuery(id+"F0.wireOp",EDGE,"E12.bottom"),sQuery(id+"F0.wireOp",EDGE,"E12.left"),sQuery(id+"F0.wireOp",EDGE,"E12.right"),sQuery(id+"F0.wireOp",EDGE,"E13.filletArc"),sQuery(id+"F0.wireOp",EDGE,"E14.filletArc"),sQuery(id+"F0.wireOp",EDGE,"E27"),sQuery(id+"F0.wireOp",EDGE,"E28"),sQuery(id+"F0.wireOp",EDGE,"E29"),sQuery(id+"F0.wireOp",EDGE,"E30"),sQuery(id+"F0.wireOp",EDGE,"E31")])],"isStart":false});
            var sketch = newSketch(context, id + "F6", { "sketchPlane" : qUnion([Q0])});
            skPoint(sketch, "E98.0", {"position": v(-65, 65) * mm});
            skPoint(sketch, "E98.1", {"position": v(65, -65) * mm});
            skLineSegment(sketch, "E99.top", {"start": v(-58.5, -65) * mm, "end": v(58.5, -65) * mm});
            skLineSegment(sketch, "E99.left", {"start": v(-58.5, 2.5) * mm, "end": v(-58.5, -65) * mm});
            skLineSegment(sketch, "E99.right", {"start": v(58.5, 2.5) * mm, "end": v(58.5, -65) * mm});
            skLineSegment(sketch, "E100.bottom", {"start": v(-32.5, -10) * mm, "end": v(32.5, -10) * mm});
            skLineSegment(sketch, "E100.top", {"start": v(-32.5, -65) * mm, "end": v(32.5, -65) * mm});
            skLineSegment(sketch, "E100.left", {"start": v(-32.5, -10) * mm, "end": v(-32.5, -65) * mm});
            skLineSegment(sketch, "E100.right", {"start": v(32.5, -10) * mm, "end": v(32.5, -65) * mm});
            skPoint(sketch, "E101.0", {"position": v(-56.5, 6.5) * mm});
            skPoint(sketch, "E102.3", {"position": v(30.54, 32.33) * mm});
            skPoint(sketch, "E103.0", {"position": v(-26.5, 33.5) * mm});
            skLineSegment(sketch, "E104", {"start": v(-58.5, 2.5) * mm, "end": v(-26.5, 2.5) * mm});
            skPoint(sketch, "E105.0", {"position": v(26.5, 33.5) * mm});
            skLineSegment(sketch, "E106", {"start": v(58.5, 2.5) * mm, "end": v(26.5, 2.5) * mm});
            skLineSegment(sketch, "E107", {"start": v(17, 16) * mm, "end": v(-17, 16) * mm});
            skLineSegment(sketch, "E108", {"start": v(-26.5, 2.5) * mm, "end": v(-26.5, 16) * mm});
            skLineSegment(sketch, "E109", {"start": v(26.5, 2.5) * mm, "end": v(26.5, 16) * mm});
            skLineSegment(sketch, "E110", {"start": v(26.5, 16) * mm, "end": v(17, 16) * mm});
            skLineSegment(sketch, "E111", {"start": v(-17, 16) * mm, "end": v(-26.5, 16) * mm});
            skSolve(sketch);
        }
        {
            var Q0;
            {var subQ6=sQuery(id+"F6.wireOp",EDGE,"E99.left");Q0=makeQuery(id+"F6.imprint","IMPRINT",FACE,{"disambiguationData":[TD([[makeQuery(id+"F6.imprint","IMPRINT",EDGE,{"derivedFrom":subQ6}),1.0]])]});}
            extrude(context, id + "F7", {"entities" : qUnion([Q0]), "operationType" : NewBodyOperationType.REMOVE, "oppositeDirection" : true, "depth" : 3.5 * mm});
        }
        {
            var Q0;
            Q0=makeQuery(id+"F1.opExtrude","CAP_FACE",FACE,{"disambiguationData":[OSD([sQuery(id+"F0.wireOp",EDGE,"E0.bottom"),sQuery(id+"F0.wireOp",EDGE,"E0.top"),sQuery(id+"F0.wireOp",EDGE,"E0.left"),sQuery(id+"F0.wireOp",EDGE,"E0.right"),sQuery(id+"F0.wireOp",EDGE,"E3"),sQuery(id+"F0.wireOp",EDGE,"E4"),sQuery(id+"F0.wireOp",EDGE,"E5"),sQuery(id+"F0.wireOp",EDGE,"E6"),sQuery(id+"F0.wireOp",EDGE,"E7"),sQuery(id+"F0.wireOp",EDGE,"E8"),sQuery(id+"F0.wireOp",EDGE,"E9.bottom"),sQuery(id+"F0.wireOp",EDGE,"E9.left"),sQuery(id+"F0.wireOp",EDGE,"E9.right"),sQuery(id+"F0.wireOp",EDGE,"E10.filletArc"),sQuery(id+"F0.wireOp",EDGE,"E11.filletArc"),sQuery(id+"F0.wireOp",EDGE,"E12.bottom"),sQuery(id+"F0.wireOp",EDGE,"E12.left"),sQuery(id+"F0.wireOp",EDGE,"E12.right"),sQuery(id+"F0.wireOp",EDGE,"E13.filletArc"),sQuery(id+"F0.wireOp",EDGE,"E14.filletArc"),sQuery(id+"F0.wireOp",EDGE,"E27"),sQuery(id+"F0.wireOp",EDGE,"E28"),sQuery(id+"F0.wireOp",EDGE,"E29"),sQuery(id+"F0.wireOp",EDGE,"E30"),sQuery(id+"F0.wireOp",EDGE,"E31")])],"isStart":false});
            var sketch = newSketch(context, id + "F8", { "sketchPlane" : qUnion([Q0])});
            skPoint(sketch, "E112.0", {"position": v(-43.5, 52.5) * mm});
            skPoint(sketch, "E112.1", {"position": v(-43.5, 39.5) * mm});
            skLineSegment(sketch, "E113.bottom", {"start": v(-31.5, 46.5) * mm, "end": v(-55.5, 46.5) * mm});
            skLineSegment(sketch, "E113.top", {"start": v(-31.5, 58.5) * mm, "end": v(-55.5, 58.5) * mm});
            skLineSegment(sketch, "E113.left", {"start": v(-31.5, 46.5) * mm, "end": v(-31.5, 58.5) * mm});
            skLineSegment(sketch, "E113.right", {"start": v(-55.5, 46.5) * mm, "end": v(-55.5, 58.5) * mm});
            skLineSegment(sketch, "E114.bottom", {"start": v(-31.5, 45.5) * mm, "end": v(-55.5, 45.5) * mm});
            skLineSegment(sketch, "E114.top", {"start": v(-31.5, 33.5) * mm, "end": v(-55.5, 33.5) * mm});
            skLineSegment(sketch, "E114.left", {"start": v(-31.5, 45.5) * mm, "end": v(-31.5, 33.5) * mm});
            skLineSegment(sketch, "E114.right", {"start": v(-55.5, 45.5) * mm, "end": v(-55.5, 33.5) * mm});
            skPoint(sketch, "E115.0", {"position": v(-57.5, 57.5) * mm});
            skPoint(sketch, "E115.1", {"position": v(-55.5, 47.5) * mm});
            skPoint(sketch, "E115.2", {"position": v(-31.5, 47.5) * mm});
            skPoint(sketch, "E115.3", {"position": v(-29.5, 57.5) * mm});
            skPoint(sketch, "E115.4", {"position": v(-57.5, 44.5) * mm});
            skPoint(sketch, "E115.5", {"position": v(-55.5, 34.5) * mm});
            skPoint(sketch, "E115.6", {"position": v(-31.5, 34.5) * mm});
            skPoint(sketch, "E115.7", {"position": v(-29.5, 44.5) * mm});
            skLineSegment(sketch, "E116.bottom", {"start": v(-57.5, 57.5) * mm, "end": v(-55.5, 57.5) * mm});
            skLineSegment(sketch, "E116.top", {"start": v(-57.5, 47.5) * mm, "end": v(-55.5, 47.5) * mm});
            skLineSegment(sketch, "E116.left", {"start": v(-57.5, 57.5) * mm, "end": v(-57.5, 47.5) * mm});
            skLineSegment(sketch, "E116.right", {"start": v(-55.5, 57.5) * mm, "end": v(-55.5, 47.5) * mm});
            skLineSegment(sketch, "E117.bottom", {"start": v(-29.5, 57.5) * mm, "end": v(-31.5, 57.5) * mm});
            skLineSegment(sketch, "E117.top", {"start": v(-29.5, 47.5) * mm, "end": v(-31.5, 47.5) * mm});
            skLineSegment(sketch, "E117.left", {"start": v(-29.5, 57.5) * mm, "end": v(-29.5, 47.5) * mm});
            skLineSegment(sketch, "E117.right", {"start": v(-31.5, 57.5) * mm, "end": v(-31.5, 47.5) * mm});
            skLineSegment(sketch, "E118.bottom", {"start": v(-57.5, 44.5) * mm, "end": v(-55.5, 44.5) * mm});
            skLineSegment(sketch, "E118.top", {"start": v(-57.5, 34.5) * mm, "end": v(-55.5, 34.5) * mm});
            skLineSegment(sketch, "E118.left", {"start": v(-57.5, 44.5) * mm, "end": v(-57.5, 34.5) * mm});
            skLineSegment(sketch, "E118.right", {"start": v(-55.5, 44.5) * mm, "end": v(-55.5, 34.5) * mm});
            skLineSegment(sketch, "E119.bottom", {"start": v(-29.5, 44.5) * mm, "end": v(-31.5, 44.5) * mm});
            skLineSegment(sketch, "E119.top", {"start": v(-29.5, 34.5) * mm, "end": v(-31.5, 34.5) * mm});
            skLineSegment(sketch, "E119.left", {"start": v(-29.5, 44.5) * mm, "end": v(-29.5, 34.5) * mm});
            skLineSegment(sketch, "E119.right", {"start": v(-31.5, 44.5) * mm, "end": v(-31.5, 34.5) * mm});
            skPoint(sketch, "E120.0", {"position": v(-43.5, 26.5) * mm});
            skPoint(sketch, "E120.1", {"position": v(-43.5, 13.5) * mm});
            skLineSegment(sketch, "E121.bottom", {"start": v(-31.5, 32.5) * mm, "end": v(-55.5, 32.5) * mm});
            skLineSegment(sketch, "E121.top", {"start": v(-31.5, 20.5) * mm, "end": v(-55.5, 20.5) * mm});
            skLineSegment(sketch, "E121.left", {"start": v(-31.5, 32.5) * mm, "end": v(-31.5, 20.5) * mm});
            skLineSegment(sketch, "E121.right", {"start": v(-55.5, 32.5) * mm, "end": v(-55.5, 20.5) * mm});
            skLineSegment(sketch, "E122.bottom", {"start": v(-31.5, 19.5) * mm, "end": v(-55.5, 19.5) * mm});
            skLineSegment(sketch, "E122.top", {"start": v(-31.5, 7.5) * mm, "end": v(-55.5, 7.5) * mm});
            skLineSegment(sketch, "E122.left", {"start": v(-31.5, 19.5) * mm, "end": v(-31.5, 7.5) * mm});
            skLineSegment(sketch, "E122.right", {"start": v(-55.5, 19.5) * mm, "end": v(-55.5, 7.5) * mm});
            skLineSegment(sketch, "E123.bottom", {"start": v(-55.5, 31.5) * mm, "end": v(-57.5, 31.5) * mm});
            skLineSegment(sketch, "E123.top", {"start": v(-55.5, 21.5) * mm, "end": v(-57.5, 21.5) * mm});
            skLineSegment(sketch, "E123.left", {"start": v(-55.5, 31.5) * mm, "end": v(-55.5, 21.5) * mm});
            skLineSegment(sketch, "E123.right", {"start": v(-57.5, 31.5) * mm, "end": v(-57.5, 21.5) * mm});
            skLineSegment(sketch, "E124.bottom", {"start": v(-55.5, 18.5) * mm, "end": v(-57.5, 18.5) * mm});
            skLineSegment(sketch, "E124.top", {"start": v(-55.5, 8.5) * mm, "end": v(-57.5, 8.5) * mm});
            skLineSegment(sketch, "E124.left", {"start": v(-55.5, 18.5) * mm, "end": v(-55.5, 8.5) * mm});
            skLineSegment(sketch, "E124.right", {"start": v(-57.5, 18.5) * mm, "end": v(-57.5, 8.5) * mm});
            skLineSegment(sketch, "E125.bottom", {"start": v(-31.5, 31.5) * mm, "end": v(-29.5, 31.5) * mm});
            skLineSegment(sketch, "E125.top", {"start": v(-31.5, 21.5) * mm, "end": v(-29.5, 21.5) * mm});
            skLineSegment(sketch, "E125.left", {"start": v(-31.5, 31.5) * mm, "end": v(-31.5, 21.5) * mm});
            skLineSegment(sketch, "E125.right", {"start": v(-29.5, 31.5) * mm, "end": v(-29.5, 21.5) * mm});
            skLineSegment(sketch, "E126.bottom", {"start": v(-31.5, 18.5) * mm, "end": v(-29.5, 18.5) * mm});
            skLineSegment(sketch, "E126.top", {"start": v(-31.5, 8.5) * mm, "end": v(-29.5, 8.5) * mm});
            skLineSegment(sketch, "E126.left", {"start": v(-31.5, 18.5) * mm, "end": v(-31.5, 8.5) * mm});
            skLineSegment(sketch, "E126.right", {"start": v(-29.5, 18.5) * mm, "end": v(-29.5, 8.5) * mm});
            skLineSegment(sketch, "E127.1.0.0", {"start": v(-28.5, 44.5) * mm, "end": v(-28.5, 34.5) * mm});
            skPoint(sketch, "E127.1.0.2", {"position": v(-26.5, 34.5) * mm});
            skPoint(sketch, "E127.1.0.3", {"position": v(-0.5, 44.5) * mm});
            skPoint(sketch, "E127.1.0.5", {"position": v(-14.5, 39.5) * mm});
            skLineSegment(sketch, "E127.1.0.6", {"start": v(-26.5, 57.5) * mm, "end": v(-26.5, 47.5) * mm});
            skPoint(sketch, "E127.1.0.8", {"position": v(-14.5, 52.5) * mm});
            skPoint(sketch, "E127.1.0.10", {"position": v(-0.5, 57.5) * mm});
            skPoint(sketch, "E127.1.0.14", {"position": v(-28.5, 57.5) * mm});
            skLineSegment(sketch, "E127.1.0.15", {"start": v(-0.5, 44.5) * mm, "end": v(-0.5, 34.5) * mm});
            skPoint(sketch, "E127.1.0.17", {"position": v(-28.5, 44.5) * mm});
            skPoint(sketch, "E127.1.0.18", {"position": v(-2.5, 34.5) * mm});
            skLineSegment(sketch, "E127.1.0.20", {"start": v(-0.5, 57.5) * mm, "end": v(-0.5, 47.5) * mm});
            skLineSegment(sketch, "E127.1.0.21", {"start": v(-2.5, 46.5) * mm, "end": v(-26.5, 46.5) * mm});
            skLineSegment(sketch, "E127.1.0.22", {"start": v(-2.5, 58.5) * mm, "end": v(-26.5, 58.5) * mm});
            skLineSegment(sketch, "E127.1.0.23", {"start": v(-28.5, 57.5) * mm, "end": v(-28.5, 47.5) * mm});
            skLineSegment(sketch, "E127.1.0.24", {"start": v(-2.5, 46.5) * mm, "end": v(-2.5, 58.5) * mm});
            skLineSegment(sketch, "E127.1.0.26", {"start": v(-2.5, 45.5) * mm, "end": v(-26.5, 45.5) * mm});
            skPoint(sketch, "E127.1.0.27", {"position": v(-26.5, 47.5) * mm});
            skPoint(sketch, "E127.1.0.28", {"position": v(-2.5, 47.5) * mm});
            skLineSegment(sketch, "E127.1.0.29", {"start": v(-26.5, 45.5) * mm, "end": v(-26.5, 33.5) * mm});
            skLineSegment(sketch, "E127.1.0.30", {"start": v(-2.5, 45.5) * mm, "end": v(-2.5, 33.5) * mm});
            skLineSegment(sketch, "E127.1.0.31", {"start": v(-2.5, 33.5) * mm, "end": v(-26.5, 33.5) * mm});
            skLineSegment(sketch, "E127.1.0.36", {"start": v(-2.5, 44.5) * mm, "end": v(-2.5, 34.5) * mm});
            skPoint(sketch, "E127.1.0.37", {"position": v(-14.5, 52.5) * mm});
            skPoint(sketch, "E127.1.0.39", {"position": v(-14.5, 39.5) * mm});
            skLineSegment(sketch, "E127.1.0.43", {"start": v(-26.5, 44.5) * mm, "end": v(-26.5, 34.5) * mm});
            skLineSegment(sketch, "E127.1.0.44", {"start": v(-2.5, 57.5) * mm, "end": v(-2.5, 47.5) * mm});
            skLineSegment(sketch, "E127.1.0.45", {"start": v(-26.5, 46.5) * mm, "end": v(-26.5, 58.5) * mm});
            skLineSegment(sketch, "E127.1.0.56", {"start": v(-0.5, 57.5) * mm, "end": v(-2.5, 57.5) * mm});
            skLineSegment(sketch, "E127.1.0.57", {"start": v(-0.5, 44.5) * mm, "end": v(-2.5, 44.5) * mm});
            skLineSegment(sketch, "E127.1.0.58", {"start": v(-28.5, 44.5) * mm, "end": v(-26.5, 44.5) * mm});
            skLineSegment(sketch, "E127.1.0.59", {"start": v(-0.5, 47.5) * mm, "end": v(-2.5, 47.5) * mm});
            skLineSegment(sketch, "E127.1.0.60", {"start": v(-28.5, 47.5) * mm, "end": v(-26.5, 47.5) * mm});
            skLineSegment(sketch, "E127.1.0.61", {"start": v(-28.5, 57.5) * mm, "end": v(-26.5, 57.5) * mm});
            skLineSegment(sketch, "E127.1.0.62", {"start": v(-0.5, 34.5) * mm, "end": v(-2.5, 34.5) * mm});
            skLineSegment(sketch, "E127.1.0.63", {"start": v(-28.5, 34.5) * mm, "end": v(-26.5, 34.5) * mm});
            skLineSegment(sketch, "E127.2.0.0", {"start": v(0.5, 44.5) * mm, "end": v(0.5, 34.5) * mm});
            skPoint(sketch, "E127.2.0.2", {"position": v(2.5, 34.5) * mm});
            skPoint(sketch, "E127.2.0.3", {"position": v(28.5, 44.5) * mm});
            skPoint(sketch, "E127.2.0.5", {"position": v(14.5, 39.5) * mm});
            skLineSegment(sketch, "E127.2.0.6", {"start": v(2.5, 57.5) * mm, "end": v(2.5, 47.5) * mm});
            skPoint(sketch, "E127.2.0.8", {"position": v(14.5, 52.5) * mm});
            skPoint(sketch, "E127.2.0.10", {"position": v(28.5, 57.5) * mm});
            skPoint(sketch, "E127.2.0.14", {"position": v(0.5, 57.5) * mm});
            skLineSegment(sketch, "E127.2.0.15", {"start": v(28.5, 44.5) * mm, "end": v(28.5, 34.5) * mm});
            skPoint(sketch, "E127.2.0.17", {"position": v(0.5, 44.5) * mm});
            skPoint(sketch, "E127.2.0.18", {"position": v(26.5, 34.5) * mm});
            skLineSegment(sketch, "E127.2.0.20", {"start": v(28.5, 57.5) * mm, "end": v(28.5, 47.5) * mm});
            skLineSegment(sketch, "E127.2.0.21", {"start": v(26.5, 46.5) * mm, "end": v(2.5, 46.5) * mm});
            skLineSegment(sketch, "E127.2.0.22", {"start": v(26.5, 58.5) * mm, "end": v(2.5, 58.5) * mm});
            skLineSegment(sketch, "E127.2.0.23", {"start": v(0.5, 57.5) * mm, "end": v(0.5, 47.5) * mm});
            skLineSegment(sketch, "E127.2.0.24", {"start": v(26.5, 46.5) * mm, "end": v(26.5, 58.5) * mm});
            skLineSegment(sketch, "E127.2.0.26", {"start": v(26.5, 45.5) * mm, "end": v(2.5, 45.5) * mm});
            skPoint(sketch, "E127.2.0.27", {"position": v(2.5, 47.5) * mm});
            skPoint(sketch, "E127.2.0.28", {"position": v(26.5, 47.5) * mm});
            skLineSegment(sketch, "E127.2.0.29", {"start": v(2.5, 45.5) * mm, "end": v(2.5, 33.5) * mm});
            skLineSegment(sketch, "E127.2.0.30", {"start": v(26.5, 45.5) * mm, "end": v(26.5, 33.5) * mm});
            skLineSegment(sketch, "E127.2.0.31", {"start": v(26.5, 33.5) * mm, "end": v(2.5, 33.5) * mm});
            skLineSegment(sketch, "E127.2.0.36", {"start": v(26.5, 44.5) * mm, "end": v(26.5, 34.5) * mm});
            skPoint(sketch, "E127.2.0.37", {"position": v(14.5, 52.5) * mm});
            skPoint(sketch, "E127.2.0.39", {"position": v(14.5, 39.5) * mm});
            skLineSegment(sketch, "E127.2.0.43", {"start": v(2.5, 44.5) * mm, "end": v(2.5, 34.5) * mm});
            skLineSegment(sketch, "E127.2.0.44", {"start": v(26.5, 57.5) * mm, "end": v(26.5, 47.5) * mm});
            skLineSegment(sketch, "E127.2.0.45", {"start": v(2.5, 46.5) * mm, "end": v(2.5, 58.5) * mm});
            skLineSegment(sketch, "E127.2.0.56", {"start": v(28.5, 57.5) * mm, "end": v(26.5, 57.5) * mm});
            skLineSegment(sketch, "E127.2.0.57", {"start": v(28.5, 44.5) * mm, "end": v(26.5, 44.5) * mm});
            skLineSegment(sketch, "E127.2.0.58", {"start": v(0.5, 44.5) * mm, "end": v(2.5, 44.5) * mm});
            skLineSegment(sketch, "E127.2.0.59", {"start": v(28.5, 47.5) * mm, "end": v(26.5, 47.5) * mm});
            skLineSegment(sketch, "E127.2.0.60", {"start": v(0.5, 47.5) * mm, "end": v(2.5, 47.5) * mm});
            skLineSegment(sketch, "E127.2.0.61", {"start": v(0.5, 57.5) * mm, "end": v(2.5, 57.5) * mm});
            skLineSegment(sketch, "E127.2.0.62", {"start": v(28.5, 34.5) * mm, "end": v(26.5, 34.5) * mm});
            skLineSegment(sketch, "E127.2.0.63", {"start": v(0.5, 34.5) * mm, "end": v(2.5, 34.5) * mm});
            skLineSegment(sketch, "E127.direction1", {"start": v(-57.5, 8.5) * mm, "end": v(-28.5, 8.5) * mm, "construction": true});
            skLineSegment(sketch, "E128.0.3.0", {"start": v(29.5, 44.5) * mm, "end": v(29.5, 34.5) * mm});
            skLineSegment(sketch, "E128.3.3.0", {"start": v(31.5, 19.5) * mm, "end": v(31.5, 7.5) * mm});
            skPoint(sketch, "E128.6.3.0", {"position": v(31.5, 34.5) * mm});
            skPoint(sketch, "E128.7.3.0", {"position": v(57.5, 44.5) * mm});
            skLineSegment(sketch, "E128.8.3.0", {"start": v(55.5, 20.5) * mm, "end": v(31.5, 20.5) * mm});
            skPoint(sketch, "E128.11.3.0", {"position": v(43.5, 39.5) * mm});
            skLineSegment(sketch, "E128.12.3.0", {"start": v(31.5, 57.5) * mm, "end": v(31.5, 47.5) * mm});
            skLineSegment(sketch, "E128.15.3.0", {"start": v(29.5, 18.5) * mm, "end": v(29.5, 8.5) * mm});
            skPoint(sketch, "E128.18.3.0", {"position": v(43.5, 52.5) * mm});
            skLineSegment(sketch, "E128.19.3.0", {"start": v(29.5, 31.5) * mm, "end": v(29.5, 21.5) * mm});
            skPoint(sketch, "E128.22.3.0", {"position": v(57.5, 57.5) * mm});
            skLineSegment(sketch, "E128.23.3.0", {"start": v(55.5, 7.5) * mm, "end": v(31.5, 7.5) * mm});
            skLineSegment(sketch, "E128.26.3.0", {"start": v(55.5, 31.5) * mm, "end": v(55.5, 21.5) * mm});
            skLineSegment(sketch, "E128.29.3.0", {"start": v(57.5, 18.5) * mm, "end": v(57.5, 8.5) * mm});
            skPoint(sketch, "E128.32.3.0", {"position": v(29.5, 57.5) * mm});
            skLineSegment(sketch, "E128.33.3.0", {"start": v(57.5, 44.5) * mm, "end": v(57.5, 34.5) * mm});
            skLineSegment(sketch, "E128.36.3.0", {"start": v(55.5, 32.5) * mm, "end": v(31.5, 32.5) * mm});
            skPoint(sketch, "E128.39.3.0", {"position": v(29.5, 44.5) * mm});
            skPoint(sketch, "E128.40.3.0", {"position": v(55.5, 34.5) * mm});
            skPoint(sketch, "E128.41.3.0", {"position": v(43.5, 13.5) * mm});
            skLineSegment(sketch, "E128.42.3.0", {"start": v(57.5, 57.5) * mm, "end": v(57.5, 47.5) * mm});
            skLineSegment(sketch, "E128.45.3.0", {"start": v(55.5, 46.5) * mm, "end": v(31.5, 46.5) * mm});
            skLineSegment(sketch, "E128.48.3.0", {"start": v(55.5, 58.5) * mm, "end": v(31.5, 58.5) * mm});
            skLineSegment(sketch, "E128.51.3.0", {"start": v(29.5, 57.5) * mm, "end": v(29.5, 47.5) * mm});
            skLineSegment(sketch, "E128.54.3.0", {"start": v(55.5, 46.5) * mm, "end": v(55.5, 58.5) * mm});
            skLineSegment(sketch, "E128.57.3.0", {"start": v(31.5, 32.5) * mm, "end": v(31.5, 20.5) * mm});
            skLineSegment(sketch, "E128.60.3.0", {"start": v(55.5, 45.5) * mm, "end": v(31.5, 45.5) * mm});
            skPoint(sketch, "E128.63.3.0", {"position": v(31.5, 47.5) * mm});
            skPoint(sketch, "E128.64.3.0", {"position": v(55.5, 47.5) * mm});
            skLineSegment(sketch, "E128.65.3.0", {"start": v(31.5, 45.5) * mm, "end": v(31.5, 33.5) * mm});
            skLineSegment(sketch, "E128.68.3.0", {"start": v(55.5, 45.5) * mm, "end": v(55.5, 33.5) * mm});
            skLineSegment(sketch, "E128.71.3.0", {"start": v(55.5, 33.5) * mm, "end": v(31.5, 33.5) * mm});
            skLineSegment(sketch, "E128.74.3.0", {"start": v(57.5, 31.5) * mm, "end": v(57.5, 21.5) * mm});
            skLineSegment(sketch, "E128.77.3.0", {"start": v(55.5, 19.5) * mm, "end": v(31.5, 19.5) * mm});
            skLineSegment(sketch, "E128.80.3.0", {"start": v(55.5, 19.5) * mm, "end": v(55.5, 7.5) * mm});
            skPoint(sketch, "E128.83.3.0", {"position": v(43.5, 26.5) * mm});
            skLineSegment(sketch, "E128.84.3.0", {"start": v(55.5, 44.5) * mm, "end": v(55.5, 34.5) * mm});
            skPoint(sketch, "E128.87.3.0", {"position": v(43.5, 52.5) * mm});
            skLineSegment(sketch, "E128.88.3.0", {"start": v(31.5, 31.5) * mm, "end": v(31.5, 21.5) * mm});
            skPoint(sketch, "E128.91.3.0", {"position": v(43.5, 39.5) * mm});
            skLineSegment(sketch, "E128.92.3.0", {"start": v(55.5, 32.5) * mm, "end": v(55.5, 20.5) * mm});
            skLineSegment(sketch, "E128.95.3.0", {"start": v(31.5, 18.5) * mm, "end": v(31.5, 8.5) * mm});
            skPoint(sketch, "E128.98.3.0", {"position": v(43.5, 13.5) * mm});
            skLineSegment(sketch, "E128.99.3.0", {"start": v(31.5, 44.5) * mm, "end": v(31.5, 34.5) * mm});
            skLineSegment(sketch, "E128.102.3.0", {"start": v(55.5, 57.5) * mm, "end": v(55.5, 47.5) * mm});
            skLineSegment(sketch, "E128.105.3.0", {"start": v(31.5, 46.5) * mm, "end": v(31.5, 58.5) * mm});
            skPoint(sketch, "E128.108.3.0", {"position": v(43.5, 26.5) * mm});
            skLineSegment(sketch, "E128.109.3.0", {"start": v(55.5, 18.5) * mm, "end": v(55.5, 8.5) * mm});
            skLineSegment(sketch, "E128.112.3.0", {"start": v(55.5, 21.5) * mm, "end": v(57.5, 21.5) * mm});
            skLineSegment(sketch, "E128.115.3.0", {"start": v(31.5, 18.5) * mm, "end": v(29.5, 18.5) * mm});
            skLineSegment(sketch, "E128.118.3.0", {"start": v(31.5, 21.5) * mm, "end": v(29.5, 21.5) * mm});
            skLineSegment(sketch, "E128.121.3.0", {"start": v(55.5, 31.5) * mm, "end": v(57.5, 31.5) * mm});
            skLineSegment(sketch, "E128.124.3.0", {"start": v(31.5, 31.5) * mm, "end": v(29.5, 31.5) * mm});
            skLineSegment(sketch, "E128.127.3.0", {"start": v(55.5, 8.5) * mm, "end": v(57.5, 8.5) * mm});
            skLineSegment(sketch, "E128.130.3.0", {"start": v(55.5, 18.5) * mm, "end": v(57.5, 18.5) * mm});
            skLineSegment(sketch, "E128.133.3.0", {"start": v(31.5, 8.5) * mm, "end": v(29.5, 8.5) * mm});
            skLineSegment(sketch, "E128.136.3.0", {"start": v(57.5, 57.5) * mm, "end": v(55.5, 57.5) * mm});
            skLineSegment(sketch, "E128.139.3.0", {"start": v(57.5, 44.5) * mm, "end": v(55.5, 44.5) * mm});
            skLineSegment(sketch, "E128.142.3.0", {"start": v(29.5, 44.5) * mm, "end": v(31.5, 44.5) * mm});
            skLineSegment(sketch, "E128.145.3.0", {"start": v(57.5, 47.5) * mm, "end": v(55.5, 47.5) * mm});
            skLineSegment(sketch, "E128.148.3.0", {"start": v(29.5, 47.5) * mm, "end": v(31.5, 47.5) * mm});
            skLineSegment(sketch, "E128.151.3.0", {"start": v(29.5, 57.5) * mm, "end": v(31.5, 57.5) * mm});
            skLineSegment(sketch, "E128.154.3.0", {"start": v(57.5, 34.5) * mm, "end": v(55.5, 34.5) * mm});
            skLineSegment(sketch, "E128.157.3.0", {"start": v(29.5, 34.5) * mm, "end": v(31.5, 34.5) * mm});
            skPoint(sketch, "E129.0", {"position": v(0, 26.33) * mm});
            skLineSegment(sketch, "E130.bottom", {"start": v(12, 19.5) * mm, "end": v(-12, 19.5) * mm});
            skLineSegment(sketch, "E130.top", {"start": v(12, 31.5) * mm, "end": v(-12, 31.5) * mm});
            skLineSegment(sketch, "E130.left", {"start": v(12, 19.5) * mm, "end": v(12, 31.5) * mm});
            skLineSegment(sketch, "E130.right", {"start": v(-12, 19.5) * mm, "end": v(-12, 31.5) * mm});
            skPoint(sketch, "E130.middle", {"position": v(0, 25.5) * mm});
            skLineSegment(sketch, "E131.bottom", {"start": v(-12, 30.5) * mm, "end": v(-14, 30.5) * mm});
            skLineSegment(sketch, "E131.top", {"start": v(-12, 20.5) * mm, "end": v(-14, 20.5) * mm});
            skLineSegment(sketch, "E131.left", {"start": v(-12, 30.5) * mm, "end": v(-12, 20.5) * mm});
            skLineSegment(sketch, "E131.right", {"start": v(-14, 30.5) * mm, "end": v(-14, 20.5) * mm});
            skLineSegment(sketch, "E132.bottom", {"start": v(12, 30.5) * mm, "end": v(14, 30.5) * mm});
            skLineSegment(sketch, "E132.top", {"start": v(12, 20.5) * mm, "end": v(14, 20.5) * mm});
            skLineSegment(sketch, "E132.left", {"start": v(12, 30.5) * mm, "end": v(12, 20.5) * mm});
            skLineSegment(sketch, "E132.right", {"start": v(14, 30.5) * mm, "end": v(14, 20.5) * mm});
            skSolve(sketch);
        }
        {
            var Q0;
            Q0 = qSketchRegion(id + "F8", true);
            extrude(context, id + "F9", {"entities" : qUnion([Q0]), "operationType" : NewBodyOperationType.REMOVE, "oppositeDirection" : true, "depth" : 2 * mm});
        }
        {
            var Q0;
            Q0=makeQuery(id+"F0.imprint","IMPRINT",FACE,{"disambiguationData":[TD([[makeQuery(id+"F0.imprint","IMPRINT",EDGE,{"derivedFrom":sQuery(id+"F0.wireOp",EDGE,"E0.bottom")}),-1.0]])]});
            var sketch = newSketch(context, id + "F10", { "sketchPlane" : qUnion([Q0])});
            skPoint(sketch, "E133.0", {"position": v(65, -65) * mm});
            skPoint(sketch, "E134.0", {"position": v(-44, -17) * mm});
            skLineSegment(sketch, "E135.bottom", {"start": v(58.5, -5) * mm, "end": v(-58.5, -5) * mm});
            skLineSegment(sketch, "E135.top", {"start": v(58.5, -65) * mm, "end": v(-58.5, -65) * mm});
            skLineSegment(sketch, "E135.left", {"start": v(58.5, -5) * mm, "end": v(58.5, -65) * mm});
            skLineSegment(sketch, "E135.right", {"start": v(-58.5, -5) * mm, "end": v(-58.5, -65) * mm});
            skCircle(sketch, "E136.0", {"center": v(0, 3) * mm, "radius": 3.5 * mm});
            skLineSegment(sketch, "E137.bottom", {"start": v(9, 12) * mm, "end": v(-9, 12) * mm});
            skLineSegment(sketch, "E137.top", {"start": v(9, -6) * mm, "end": v(-9, -6) * mm});
            skLineSegment(sketch, "E137.left", {"start": v(9, 12) * mm, "end": v(9, -6) * mm});
            skLineSegment(sketch, "E137.right", {"start": v(-9, 12) * mm, "end": v(-9, -6) * mm});
            skSolve(sketch);
        }
        {
            var Q0;
            Q0 = qSketchRegion(id + "F10", true);
            extrude(context, id + "F11", {"entities" : qUnion([Q0]), "operationType" : NewBodyOperationType.REMOVE, "depth" : 5.5 * mm});
        }
        {
            var Q0;
            Q0=makeQuery(id+"F11.boolean.opBoolean","COPY",FACE,{"derivedFrom":makeQuery(id+"F11.opExtrude","CAP_FACE",FACE,{"disambiguationData":[OSD([sQuery(id+"F10.wireOp",EDGE,"E135.bottom"),sQuery(id+"F10.wireOp",EDGE,"E135.top"),sQuery(id+"F10.wireOp",EDGE,"E135.left"),sQuery(id+"F10.wireOp",EDGE,"E135.right")])],"isStart":false})});
            var sketch = newSketch(context, id + "F12", { "sketchPlane" : qUnion([Q0])});
            skLineSegment(sketch, "E138.0", {"start": v(-27.5, 21.5) * mm, "end": v(-14.5, 21.5) * mm});
            skLineSegment(sketch, "E138.1", {"start": v(-14.5, 21.5) * mm, "end": v(-14.5, 40) * mm});
            skLineSegment(sketch, "E138.2", {"start": v(-27.5, 21.5) * mm, "end": v(-27.5, 40) * mm});
            skArc(sketch, "E138.3", {"start": v(-27.5, 40) * mm, "mid": v(-21, 46.5) * mm, "end": v(-14.5, 40) * mm});
            skArc(sketch, "E139", {"start": v(-14.5, 40) * mm, "mid": v(-21, 46.5) * mm, "end": v(-27.5, 40) * mm});
            skCircle(sketch, "E140", {"center": v(-21, 40) * mm, "radius": 5.5 * mm});
            skLineSegment(sketch, "E141.0", {"start": v(-26.5, 22.5) * mm, "end": v(-26.5, 40) * mm});
            skLineSegment(sketch, "E141.1", {"start": v(-26.5, 22.5) * mm, "end": v(-15.5, 22.5) * mm});
            skLineSegment(sketch, "E141.2", {"start": v(-15.5, 22.5) * mm, "end": v(-15.5, 40) * mm});
            skLineSegment(sketch, "E142.1.0.0", {"start": v(14.5, 21.5) * mm, "end": v(27.5, 21.5) * mm});
            skLineSegment(sketch, "E142.1.0.1", {"start": v(14.5, 21.5) * mm, "end": v(14.5, 40) * mm});
            skLineSegment(sketch, "E142.1.0.2", {"start": v(27.5, 21.5) * mm, "end": v(27.5, 40) * mm});
            skArc(sketch, "E142.1.0.3", {"start": v(27.5, 40) * mm, "mid": v(21, 46.5) * mm, "end": v(14.5, 40) * mm});
            skCircle(sketch, "E142.1.0.4", {"center": v(21, 40) * mm, "radius": 5.5 * mm});
            skLineSegment(sketch, "E142.1.0.5", {"start": v(15.5, 22.5) * mm, "end": v(15.5, 40) * mm});
            skLineSegment(sketch, "E142.1.0.6", {"start": v(15.5, 22.5) * mm, "end": v(26.5, 22.5) * mm});
            skLineSegment(sketch, "E142.1.0.7", {"start": v(26.5, 22.5) * mm, "end": v(26.5, 40) * mm});
            skLineSegment(sketch, "E142.1.0.8", {"start": v(14.5, 21.5) * mm, "end": v(14.5, 40) * mm});
            skArc(sketch, "E142.1.0.9", {"start": v(14.5, 40) * mm, "mid": v(21, 46.5) * mm, "end": v(27.5, 40) * mm});
            skLineSegment(sketch, "E142.1.0.10", {"start": v(27.5, 21.5) * mm, "end": v(27.5, 40) * mm});
            skLineSegment(sketch, "E142.1.0.11", {"start": v(14.5, 21.5) * mm, "end": v(27.5, 21.5) * mm});
            skLineSegment(sketch, "E142.direction1", {"start": v(-27.5, 21.5) * mm, "end": v(14.5, 21.5) * mm, "construction": true});
            skCircle(sketch, "E143", {"center": v(0, 49) * mm, "radius": 6 * mm});
            skCircle(sketch, "E144", {"center": v(0, 49) * mm, "radius": 5 * mm});
            skSolve(sketch);
        }
        {
            var Q0;
            Q0 = qSketchRegion(id + "F12", true);
            extrude(context, id + "F13", {"entities" : qUnion([Q0]), "operationType" : NewBodyOperationType.ADD, "oppositeDirection" : true, "depth" : 3.5 * mm});
        }
        {
            var Q0;
            Q0=makeQuery(id+"F7.boolean.opBoolean","COPY",FACE,{"derivedFrom":makeQuery(id+"F7.opExtrude","CAP_FACE",FACE,{"disambiguationData":[OSD([sQuery(id+"F0.wireOp",EDGE,"E3"),sQuery(id+"F0.wireOp",EDGE,"E4"),sQuery(id+"F0.wireOp",EDGE,"E5"),sQuery(id+"F0.wireOp",EDGE,"E6"),sQuery(id+"F0.wireOp",EDGE,"E31"),sQuery(id+"F6.wireOp",EDGE,"E99.top"),sQuery(id+"F6.wireOp",EDGE,"E99.left"),sQuery(id+"F6.wireOp",EDGE,"E99.right"),sQuery(id+"F6.wireOp",EDGE,"E100.bottom"),sQuery(id+"F6.wireOp",EDGE,"E100.left"),sQuery(id+"F6.wireOp",EDGE,"E100.right"),sQuery(id+"F6.wireOp",EDGE,"21Ls3SQl-b2cp-nhTs-Hews-Hz9DtT0whMqm"),sQuery(id+"F6.wireOp",EDGE,"h0CnTGEP-4mNU-iRKy-m8ki-n2eBBufmcQq5"),sQuery(id+"F6.wireOp",EDGE,"qAz8Wjot-FG1B-pc5J-QFhs-qNFrgCeN3wRs"),sQuery(id+"F6.wireOp",EDGE,"3BzKvOmG-jRT5-2gjX-6HEZ-JfMvCsTB6kLf"),sQuery(id+"F6.wireOp",EDGE,"7Y8pnDtM-46dH-8U0t-9n2W-nKTeQMZVXlmL"),sQuery(id+"F6.wireOp",EDGE,"64VHZfUW-AVCi-dtqN-Gh6Z-GknAN1bG2Krn"),sQuery(id+"F6.wireOp",EDGE,"LlS92kWC-FErj-klcS-SA7n-WFnKCBPUT4uf"),sQuery(id+"F6.wireOp",EDGE,"mzuXxwp6-lihL-K5XO-aSKc-62nNCRZgz7h9"),sQuery(id+"F6.wireOp",EDGE,"WjnmBHCa-nJvr-w590-o91h-GlZ44agCWnqu"),sQuery(id+"F6.wireOp",EDGE,"ubTacVJG-JOSL-nPcE-mceO-RuthxvDxnQcS")])],"isStart":false})});
            var sketch = newSketch(context, id + "F14", { "sketchPlane" : qUnion([Q0])});
            skPoint(sketch, "E145.0", {"position": v(-62, -65) * mm});
            skPoint(sketch, "E145.1", {"position": v(32.5, -65) * mm});
            skPoint(sketch, "E145.2", {"position": v(-32.5, -65) * mm});
            skPoint(sketch, "E145.3", {"position": v(62, -65) * mm});
            skLineSegment(sketch, "E146.bottom", {"start": v(-62, -30.5) * mm, "end": v(-32.5, -30.5) * mm});
            skLineSegment(sketch, "E146.top", {"start": v(-62, -35.5) * mm, "end": v(-32.5, -35.5) * mm});
            skLineSegment(sketch, "E146.left", {"start": v(-62, -30.5) * mm, "end": v(-62, -35.5) * mm});
            skLineSegment(sketch, "E146.right", {"start": v(-32.5, -30.5) * mm, "end": v(-32.5, -35.5) * mm});
            skLineSegment(sketch, "E147.bottom", {"start": v(32.5, -30.5) * mm, "end": v(62, -30.5) * mm});
            skLineSegment(sketch, "E147.top", {"start": v(32.5, -35.5) * mm, "end": v(62, -35.5) * mm});
            skLineSegment(sketch, "E147.left", {"start": v(32.5, -30.5) * mm, "end": v(32.5, -35.5) * mm});
            skLineSegment(sketch, "E147.right", {"start": v(62, -30.5) * mm, "end": v(62, -35.5) * mm});
            skSolve(sketch);
        }
        {
            var Q0;
            Q0 = qSketchRegion(id + "F14", true);
            extrude(context, id + "F15", {"entities" : qUnion([Q0]), "operationType" : NewBodyOperationType.ADD, "depth" : 3.5 * mm});
        }
        {
            var Q0;
            {var subQ3=sQuery(id+"F8.wireOp",EDGE,"E113.bottom");Q0=makeQuery(id+"F8.imprint","IMPRINT",FACE,{"disambiguationData":[TD([[makeQuery(id+"F8.imprint","IMPRINT",EDGE,{"derivedFrom":subQ3}),-1.0]])]});}
            var sketch = newSketch(context, id + "F16", { "sketchPlane" : qUnion([Q0])});
            skPoint(sketch, "E148.0", {"position": v(-55.5, 52.5) * mm});
            skPoint(sketch, "E148.1", {"position": v(-31.5, 52.5) * mm});
            skLineSegment(sketch, "E149.bottom", {"start": v(-55.5, 56.5) * mm, "end": v(-31.5, 56.5) * mm});
            skLineSegment(sketch, "E149.top", {"start": v(-55.5, 54.5) * mm, "end": v(-31.5, 54.5) * mm});
            skLineSegment(sketch, "E149.left", {"start": v(-55.5, 56.5) * mm, "end": v(-55.5, 54.5) * mm});
            skLineSegment(sketch, "E149.right", {"start": v(-31.5, 56.5) * mm, "end": v(-31.5, 54.5) * mm});
            skLineSegment(sketch, "E150.bottom", {"start": v(-55.5, 50.5) * mm, "end": v(-31.5, 50.5) * mm});
            skLineSegment(sketch, "E150.top", {"start": v(-55.5, 48.5) * mm, "end": v(-31.5, 48.5) * mm});
            skLineSegment(sketch, "E150.left", {"start": v(-55.5, 50.5) * mm, "end": v(-55.5, 48.5) * mm});
            skLineSegment(sketch, "E150.right", {"start": v(-31.5, 50.5) * mm, "end": v(-31.5, 48.5) * mm});
            skLineSegment(sketch, "E151.bottom", {"start": v(-55.5, 43.5) * mm, "end": v(-31.5, 43.5) * mm});
            skLineSegment(sketch, "E151.top", {"start": v(-55.5, 41.5) * mm, "end": v(-31.5, 41.5) * mm});
            skLineSegment(sketch, "E151.left", {"start": v(-55.5, 43.5) * mm, "end": v(-55.5, 41.5) * mm});
            skLineSegment(sketch, "E151.right", {"start": v(-31.5, 43.5) * mm, "end": v(-31.5, 41.5) * mm});
            skLineSegment(sketch, "E152.bottom", {"start": v(-55.5, 37.5) * mm, "end": v(-31.5, 37.5) * mm});
            skLineSegment(sketch, "E152.top", {"start": v(-55.5, 35.5) * mm, "end": v(-31.5, 35.5) * mm});
            skLineSegment(sketch, "E152.left", {"start": v(-55.5, 37.5) * mm, "end": v(-55.5, 35.5) * mm});
            skLineSegment(sketch, "E152.right", {"start": v(-31.5, 37.5) * mm, "end": v(-31.5, 35.5) * mm});
            skLineSegment(sketch, "E153.bottom", {"start": v(-55.5, 30.5) * mm, "end": v(-31.5, 30.5) * mm});
            skLineSegment(sketch, "E153.top", {"start": v(-55.5, 28.5) * mm, "end": v(-31.5, 28.5) * mm});
            skLineSegment(sketch, "E153.left", {"start": v(-55.5, 30.5) * mm, "end": v(-55.5, 28.5) * mm});
            skLineSegment(sketch, "E153.right", {"start": v(-31.5, 30.5) * mm, "end": v(-31.5, 28.5) * mm});
            skLineSegment(sketch, "E154.bottom", {"start": v(-55.5, 24.5) * mm, "end": v(-31.5, 24.5) * mm});
            skLineSegment(sketch, "E154.top", {"start": v(-55.5, 22.5) * mm, "end": v(-31.5, 22.5) * mm});
            skLineSegment(sketch, "E154.left", {"start": v(-55.5, 24.5) * mm, "end": v(-55.5, 22.5) * mm});
            skLineSegment(sketch, "E154.right", {"start": v(-31.5, 24.5) * mm, "end": v(-31.5, 22.5) * mm});
            skLineSegment(sketch, "E155.bottom", {"start": v(-55.5, 17.5) * mm, "end": v(-31.5, 17.5) * mm});
            skLineSegment(sketch, "E155.top", {"start": v(-55.5, 15.5) * mm, "end": v(-31.5, 15.5) * mm});
            skLineSegment(sketch, "E155.left", {"start": v(-55.5, 17.5) * mm, "end": v(-55.5, 15.5) * mm});
            skLineSegment(sketch, "E155.right", {"start": v(-31.5, 17.5) * mm, "end": v(-31.5, 15.5) * mm});
            skLineSegment(sketch, "E156.bottom", {"start": v(-55.5, 11.5) * mm, "end": v(-31.5, 11.5) * mm});
            skLineSegment(sketch, "E156.top", {"start": v(-55.5, 9.5) * mm, "end": v(-31.5, 9.5) * mm});
            skLineSegment(sketch, "E156.left", {"start": v(-55.5, 11.5) * mm, "end": v(-55.5, 9.5) * mm});
            skLineSegment(sketch, "E156.right", {"start": v(-31.5, 11.5) * mm, "end": v(-31.5, 9.5) * mm});
            skLineSegment(sketch, "E157.1.0.0", {"start": v(-26.5, 41.5) * mm, "end": v(-2.5, 41.5) * mm});
            skLineSegment(sketch, "E157.1.0.1", {"start": v(-26.5, 43.5) * mm, "end": v(-2.5, 43.5) * mm});
            skLineSegment(sketch, "E157.1.0.2", {"start": v(-26.5, 48.5) * mm, "end": v(-2.5, 48.5) * mm});
            skLineSegment(sketch, "E157.1.0.4", {"start": v(-26.5, 37.5) * mm, "end": v(-2.5, 37.5) * mm});
            skLineSegment(sketch, "E157.1.0.6", {"start": v(-26.5, 50.5) * mm, "end": v(-2.5, 50.5) * mm});
            skLineSegment(sketch, "E157.1.0.7", {"start": v(-26.5, 54.5) * mm, "end": v(-2.5, 54.5) * mm});
            skLineSegment(sketch, "E157.1.0.8", {"start": v(-26.5, 56.5) * mm, "end": v(-2.5, 56.5) * mm});
            skLineSegment(sketch, "E157.1.0.11", {"start": v(-26.5, 35.5) * mm, "end": v(-2.5, 35.5) * mm});
            skPoint(sketch, "E157.1.0.13", {"position": v(-2.5, 52.5) * mm});
            skPoint(sketch, "E157.1.0.16", {"position": v(-26.5, 52.5) * mm});
            skLineSegment(sketch, "E157.1.0.18", {"start": v(-2.5, 50.5) * mm, "end": v(-2.5, 48.5) * mm});
            skLineSegment(sketch, "E157.1.0.19", {"start": v(-26.5, 50.5) * mm, "end": v(-26.5, 48.5) * mm});
            skLineSegment(sketch, "E157.1.0.21", {"start": v(-2.5, 43.5) * mm, "end": v(-2.5, 41.5) * mm});
            skLineSegment(sketch, "E157.1.0.25", {"start": v(-2.5, 56.5) * mm, "end": v(-2.5, 54.5) * mm});
            skLineSegment(sketch, "E157.1.0.26", {"start": v(-26.5, 56.5) * mm, "end": v(-26.5, 54.5) * mm});
            skLineSegment(sketch, "E157.1.0.28", {"start": v(-2.5, 37.5) * mm, "end": v(-2.5, 35.5) * mm});
            skLineSegment(sketch, "E157.1.0.29", {"start": v(-26.5, 37.5) * mm, "end": v(-26.5, 35.5) * mm});
            skLineSegment(sketch, "E157.1.0.30", {"start": v(-26.5, 43.5) * mm, "end": v(-26.5, 41.5) * mm});
            skLineSegment(sketch, "E157.2.0.0", {"start": v(2.5, 41.5) * mm, "end": v(26.5, 41.5) * mm});
            skLineSegment(sketch, "E157.2.0.1", {"start": v(2.5, 43.5) * mm, "end": v(26.5, 43.5) * mm});
            skLineSegment(sketch, "E157.2.0.2", {"start": v(2.5, 48.5) * mm, "end": v(26.5, 48.5) * mm});
            skLineSegment(sketch, "E157.2.0.4", {"start": v(2.5, 37.5) * mm, "end": v(26.5, 37.5) * mm});
            skLineSegment(sketch, "E157.2.0.6", {"start": v(2.5, 50.5) * mm, "end": v(26.5, 50.5) * mm});
            skLineSegment(sketch, "E157.2.0.7", {"start": v(2.5, 54.5) * mm, "end": v(26.5, 54.5) * mm});
            skLineSegment(sketch, "E157.2.0.8", {"start": v(2.5, 56.5) * mm, "end": v(26.5, 56.5) * mm});
            skLineSegment(sketch, "E157.2.0.11", {"start": v(2.5, 35.5) * mm, "end": v(26.5, 35.5) * mm});
            skPoint(sketch, "E157.2.0.13", {"position": v(26.5, 52.5) * mm});
            skPoint(sketch, "E157.2.0.16", {"position": v(2.5, 52.5) * mm});
            skLineSegment(sketch, "E157.2.0.18", {"start": v(26.5, 50.5) * mm, "end": v(26.5, 48.5) * mm});
            skLineSegment(sketch, "E157.2.0.19", {"start": v(2.5, 50.5) * mm, "end": v(2.5, 48.5) * mm});
            skLineSegment(sketch, "E157.2.0.21", {"start": v(26.5, 43.5) * mm, "end": v(26.5, 41.5) * mm});
            skLineSegment(sketch, "E157.2.0.25", {"start": v(26.5, 56.5) * mm, "end": v(26.5, 54.5) * mm});
            skLineSegment(sketch, "E157.2.0.26", {"start": v(2.5, 56.5) * mm, "end": v(2.5, 54.5) * mm});
            skLineSegment(sketch, "E157.2.0.28", {"start": v(26.5, 37.5) * mm, "end": v(26.5, 35.5) * mm});
            skLineSegment(sketch, "E157.2.0.29", {"start": v(2.5, 37.5) * mm, "end": v(2.5, 35.5) * mm});
            skLineSegment(sketch, "E157.2.0.30", {"start": v(2.5, 43.5) * mm, "end": v(2.5, 41.5) * mm});
            skLineSegment(sketch, "E157.3.0.0", {"start": v(31.5, 41.5) * mm, "end": v(55.5, 41.5) * mm});
            skLineSegment(sketch, "E157.3.0.1", {"start": v(31.5, 43.5) * mm, "end": v(55.5, 43.5) * mm});
            skLineSegment(sketch, "E157.3.0.2", {"start": v(31.5, 48.5) * mm, "end": v(55.5, 48.5) * mm});
            skLineSegment(sketch, "E157.3.0.3", {"start": v(31.5, 30.5) * mm, "end": v(55.5, 30.5) * mm});
            skLineSegment(sketch, "E157.3.0.4", {"start": v(31.5, 37.5) * mm, "end": v(55.5, 37.5) * mm});
            skLineSegment(sketch, "E157.3.0.5", {"start": v(31.5, 17.5) * mm, "end": v(55.5, 17.5) * mm});
            skLineSegment(sketch, "E157.3.0.6", {"start": v(31.5, 50.5) * mm, "end": v(55.5, 50.5) * mm});
            skLineSegment(sketch, "E157.3.0.7", {"start": v(31.5, 54.5) * mm, "end": v(55.5, 54.5) * mm});
            skLineSegment(sketch, "E157.3.0.8", {"start": v(31.5, 56.5) * mm, "end": v(55.5, 56.5) * mm});
            skLineSegment(sketch, "E157.3.0.9", {"start": v(31.5, 28.5) * mm, "end": v(55.5, 28.5) * mm});
            skLineSegment(sketch, "E157.3.0.10", {"start": v(31.5, 11.5) * mm, "end": v(55.5, 11.5) * mm});
            skLineSegment(sketch, "E157.3.0.11", {"start": v(31.5, 35.5) * mm, "end": v(55.5, 35.5) * mm});
            skLineSegment(sketch, "E157.3.0.12", {"start": v(31.5, 22.5) * mm, "end": v(55.5, 22.5) * mm});
            skPoint(sketch, "E157.3.0.13", {"position": v(55.5, 52.5) * mm});
            skLineSegment(sketch, "E157.3.0.14", {"start": v(31.5, 9.5) * mm, "end": v(55.5, 9.5) * mm});
            skLineSegment(sketch, "E157.3.0.15", {"start": v(31.5, 24.5) * mm, "end": v(55.5, 24.5) * mm});
            skPoint(sketch, "E157.3.0.16", {"position": v(31.5, 52.5) * mm});
            skLineSegment(sketch, "E157.3.0.17", {"start": v(31.5, 15.5) * mm, "end": v(55.5, 15.5) * mm});
            skLineSegment(sketch, "E157.3.0.18", {"start": v(55.5, 50.5) * mm, "end": v(55.5, 48.5) * mm});
            skLineSegment(sketch, "E157.3.0.19", {"start": v(31.5, 50.5) * mm, "end": v(31.5, 48.5) * mm});
            skLineSegment(sketch, "E157.3.0.20", {"start": v(31.5, 24.5) * mm, "end": v(31.5, 22.5) * mm});
            skLineSegment(sketch, "E157.3.0.21", {"start": v(55.5, 43.5) * mm, "end": v(55.5, 41.5) * mm});
            skLineSegment(sketch, "E157.3.0.22", {"start": v(55.5, 11.5) * mm, "end": v(55.5, 9.5) * mm});
            skLineSegment(sketch, "E157.3.0.23", {"start": v(31.5, 30.5) * mm, "end": v(31.5, 28.5) * mm});
            skLineSegment(sketch, "E157.3.0.24", {"start": v(55.5, 17.5) * mm, "end": v(55.5, 15.5) * mm});
            skLineSegment(sketch, "E157.3.0.25", {"start": v(55.5, 56.5) * mm, "end": v(55.5, 54.5) * mm});
            skLineSegment(sketch, "E157.3.0.26", {"start": v(31.5, 56.5) * mm, "end": v(31.5, 54.5) * mm});
            skLineSegment(sketch, "E157.3.0.27", {"start": v(31.5, 11.5) * mm, "end": v(31.5, 9.5) * mm});
            skLineSegment(sketch, "E157.3.0.28", {"start": v(55.5, 37.5) * mm, "end": v(55.5, 35.5) * mm});
            skLineSegment(sketch, "E157.3.0.29", {"start": v(31.5, 37.5) * mm, "end": v(31.5, 35.5) * mm});
            skLineSegment(sketch, "E157.3.0.30", {"start": v(31.5, 43.5) * mm, "end": v(31.5, 41.5) * mm});
            skLineSegment(sketch, "E157.3.0.31", {"start": v(55.5, 24.5) * mm, "end": v(55.5, 22.5) * mm});
            skLineSegment(sketch, "E157.3.0.32", {"start": v(31.5, 17.5) * mm, "end": v(31.5, 15.5) * mm});
            skLineSegment(sketch, "E157.3.0.33", {"start": v(55.5, 30.5) * mm, "end": v(55.5, 28.5) * mm});
            skLineSegment(sketch, "E157.direction1", {"start": v(-55.5, 9.5) * mm, "end": v(-26.5, 9.5) * mm, "construction": true});
            skPoint(sketch, "E158.0", {"position": v(-12, 19.5) * mm});
            skPoint(sketch, "E158.1", {"position": v(12, 31.5) * mm});
            skLineSegment(sketch, "E159.bottom", {"start": v(-12, 27.5) * mm, "end": v(12, 27.5) * mm});
            skLineSegment(sketch, "E159.top", {"start": v(-12, 29.5) * mm, "end": v(12, 29.5) * mm});
            skLineSegment(sketch, "E159.left", {"start": v(-12, 27.5) * mm, "end": v(-12, 29.5) * mm});
            skLineSegment(sketch, "E159.right", {"start": v(12, 27.5) * mm, "end": v(12, 29.5) * mm});
            skLineSegment(sketch, "E160.bottom", {"start": v(-12, 23.5) * mm, "end": v(12, 23.5) * mm});
            skLineSegment(sketch, "E160.top", {"start": v(-12, 21.5) * mm, "end": v(12, 21.5) * mm});
            skLineSegment(sketch, "E160.left", {"start": v(-12, 23.5) * mm, "end": v(-12, 21.5) * mm});
            skLineSegment(sketch, "E160.right", {"start": v(12, 23.5) * mm, "end": v(12, 21.5) * mm});
            skSolve(sketch);
        }
        {
            var Q0;
            Q0=qCreatedBy(makeId("Top.planeOp"),FACE);
            var sketch = newSketch(context, id + "F17", { "sketchPlane" : qUnion([Q0])});
            skLineSegment(sketch, "E161.bottom", {"start": v(-43.18, 101.93) * mm, "end": v(-67.18, 101.93) * mm});
            skLineSegment(sketch, "E161.top", {"start": v(-43.18, 113.93) * mm, "end": v(-67.18, 113.93) * mm});
            skLineSegment(sketch, "E161.left", {"start": v(-43.18, 101.93) * mm, "end": v(-43.18, 113.93) * mm});
            skLineSegment(sketch, "E161.right", {"start": v(-67.18, 101.93) * mm, "end": v(-67.18, 113.93) * mm});
            skPoint(sketch, "E161.middle", {"position": v(-55.18, 107.93) * mm});
            skLineSegment(sketch, "E162.bottom", {"start": v(-67.18, 112.83) * mm, "end": v(-69.08, 112.83) * mm});
            skLineSegment(sketch, "E162.top", {"start": v(-67.18, 103.03) * mm, "end": v(-69.08, 103.03) * mm});
            skLineSegment(sketch, "E162.left", {"start": v(-67.18, 112.83) * mm, "end": v(-67.18, 103.03) * mm});
            skLineSegment(sketch, "E162.right", {"start": v(-69.08, 112.83) * mm, "end": v(-69.08, 103.03) * mm});
            skLineSegment(sketch, "E163.bottom", {"start": v(-43.18, 112.83) * mm, "end": v(-41.28, 112.83) * mm});
            skLineSegment(sketch, "E163.top", {"start": v(-43.18, 103.03) * mm, "end": v(-41.28, 103.03) * mm});
            skLineSegment(sketch, "E163.left", {"start": v(-43.18, 112.83) * mm, "end": v(-43.18, 103.03) * mm});
            skLineSegment(sketch, "E163.right", {"start": v(-41.28, 112.83) * mm, "end": v(-41.28, 103.03) * mm});
            skSolve(sketch);
        }
        {
            var Q0;
            Q0 = qSketchRegion(id + "F17", true);
            extrude(context, id + "F18", {"entities" : qUnion([Q0]), "depth" : 1.9 * mm, "offsetDistance" : 25 * mm});
        }
        {
            var Q0;
            Q0=makeQuery(id+"F18.opExtrude","CAP_FACE",FACE,{"disambiguationData":[OSD([sQuery(id+"F17.wireOp",EDGE,"E161.bottom"),sQuery(id+"F17.wireOp",EDGE,"E161.top"),sQuery(id+"F17.wireOp",EDGE,"E161.left"),sQuery(id+"F17.wireOp",EDGE,"E161.right"),sQuery(id+"F17.wireOp",EDGE,"E162.bottom"),sQuery(id+"F17.wireOp",EDGE,"E162.top"),sQuery(id+"F17.wireOp",EDGE,"E162.right"),sQuery(id+"F17.wireOp",EDGE,"E163.bottom"),sQuery(id+"F17.wireOp",EDGE,"E163.top"),sQuery(id+"F17.wireOp",EDGE,"E163.right")])],"isStart":false});
            var sketch = newSketch(context, id + "F19", { "sketchPlane" : qUnion([Q0])});
            skLineSegment(sketch, "E164.bottom", {"start": v(-67.18, 113.93) * mm, "end": v(-43.18, 113.93) * mm});
            skLineSegment(sketch, "E164.top", {"start": v(-67.18, 101.93) * mm, "end": v(-43.18, 101.93) * mm});
            skLineSegment(sketch, "E164.left", {"start": v(-67.18, 113.93) * mm, "end": v(-67.18, 101.93) * mm});
            skLineSegment(sketch, "E164.right", {"start": v(-43.18, 113.93) * mm, "end": v(-43.18, 101.93) * mm});
            skSolve(sketch);
        }
        {
            var Q0;
            Q0 = qSketchRegion(id + "F19", true);
            extrude(context, id + "F20", {"entities" : qUnion([Q0]), "operationType" : NewBodyOperationType.ADD, "depth" : 2 * mm});
        }
        {
            var Q0;
            Q0=makeQuery(id+"F20.opExtrude","CAP_FACE",FACE,{"disambiguationData":[OSD([sQuery(id+"F19.wireOp",EDGE,"E164.bottom"),sQuery(id+"F19.wireOp",EDGE,"E164.top"),sQuery(id+"F19.wireOp",EDGE,"E164.left"),sQuery(id+"F19.wireOp",EDGE,"E164.right")])],"isStart":false});
            var sketch = newSketch(context, id + "F21", { "sketchPlane" : qUnion([Q0])});
            skLineSegment(sketch, "E165.bottom", {"start": v(-44.18, 102.93) * mm, "end": v(-66.18, 102.93) * mm});
            skLineSegment(sketch, "E165.top", {"start": v(-44.18, 112.93) * mm, "end": v(-66.18, 112.93) * mm});
            skLineSegment(sketch, "E165.left", {"start": v(-44.18, 102.93) * mm, "end": v(-44.18, 112.93) * mm});
            skLineSegment(sketch, "E165.right", {"start": v(-66.18, 102.93) * mm, "end": v(-66.18, 112.93) * mm});
            skPoint(sketch, "E165.middle", {"position": v(-55.18, 107.93) * mm});
            skPoint(sketch, "E165.middle.positionSnap0", {"position": v(-55.18, 113.93) * mm});
            skPoint(sketch, "E165.middle.positionSnap1", {"position": v(-67.18, 107.93) * mm});
            skPoint(sketch, "E165.centerSnap0", {"position": v(-55.18, 113.93) * mm});
            skPoint(sketch, "E165.centerSnap1", {"position": v(-67.18, 107.93) * mm});
            skSolve(sketch);
        }
        {
            var Q0;
            Q0 = qSketchRegion(id + "F21", true);
            extrude(context, id + "F22", {"entities" : qUnion([Q0]), "operationType" : NewBodyOperationType.ADD, "depth" : 3 * mm, "offsetDistance" : 25 * mm});
        }
        {
            var Q0;
            Q0=makeQuery(id+"F18.opExtrude","CAP_FACE",FACE,{"disambiguationData":[OSD([sQuery(id+"F17.wireOp",EDGE,"E161.bottom"),sQuery(id+"F17.wireOp",EDGE,"E161.top"),sQuery(id+"F17.wireOp",EDGE,"E161.left"),sQuery(id+"F17.wireOp",EDGE,"E161.right"),sQuery(id+"F17.wireOp",EDGE,"E162.bottom"),sQuery(id+"F17.wireOp",EDGE,"E162.top"),sQuery(id+"F17.wireOp",EDGE,"E162.right"),sQuery(id+"F17.wireOp",EDGE,"E163.bottom"),sQuery(id+"F17.wireOp",EDGE,"E163.top"),sQuery(id+"F17.wireOp",EDGE,"E163.right")])],"isStart":true});
            var sketch = newSketch(context, id + "F23", { "sketchPlane" : qUnion([Q0])});
            skLineSegment(sketch, "E166.bottom", {"start": v(-44.18, -112.93) * mm, "end": v(-66.18, -112.93) * mm});
            skLineSegment(sketch, "E166.top", {"start": v(-44.18, -102.93) * mm, "end": v(-66.18, -102.93) * mm});
            skLineSegment(sketch, "E166.left", {"start": v(-44.18, -112.93) * mm, "end": v(-44.18, -102.93) * mm});
            skLineSegment(sketch, "E166.right", {"start": v(-66.18, -112.93) * mm, "end": v(-66.18, -102.93) * mm});
            skPoint(sketch, "E166.middle", {"position": v(-55.18, -107.93) * mm});
            skPoint(sketch, "E166.middle.positionSnap0", {"position": v(-55.18, -101.93) * mm});
            skPoint(sketch, "E166.middle.positionSnap1", {"position": v(-69.08, -107.93) * mm});
            skPoint(sketch, "E166.centerSnap0", {"position": v(-55.18, -101.93) * mm});
            skPoint(sketch, "E166.centerSnap1", {"position": v(-69.08, -107.93) * mm});
            skSolve(sketch);
        }
        {
            var Q0;
            Q0 = qSketchRegion(id + "F23", true);
            extrude(context, id + "F24", {"entities" : qUnion([Q0]), "operationType" : NewBodyOperationType.REMOVE, "oppositeDirection" : true, "depth" : 3 * mm});
        }
        {
            var Q0;
            Q0 = qSketchRegion(id + "F16", true);
            extrude(context, id + "F25", {"entities" : qUnion([Q0]), "operationType" : NewBodyOperationType.REMOVE, "oppositeDirection" : true, "depth" : 15 * mm});
        }
        {
            var Q0;
            Q0=makeQuery(id+"F0.imprint","IMPRINT",FACE,{"disambiguationData":[TD([[makeQuery(id+"F0.imprint","IMPRINT",EDGE,{"derivedFrom":sQuery(id+"F0.wireOp",EDGE,"E0.bottom")}),-1.0]])]});
            var sketch = newSketch(context, id + "F26", { "sketchPlane" : qUnion([Q0])});
            skLineSegment(sketch, "E167.bottom", {"start": v(60, 61) * mm, "end": v(-60, 61) * mm});
            skLineSegment(sketch, "E167.top", {"start": v(60, 2.5) * mm, "end": v(26.5, 2.5) * mm});
            skLineSegment(sketch, "E167.left", {"start": v(60, 61) * mm, "end": v(60, 2.5) * mm});
            skLineSegment(sketch, "E167.right", {"start": v(-60, 61) * mm, "end": v(-60, 2.5) * mm});
            skLineSegment(sketch, "E168.top", {"start": v(26.5, 16) * mm, "end": v(-26.5, 16) * mm});
            skLineSegment(sketch, "E168.left", {"start": v(26.5, 2.5) * mm, "end": v(26.5, 16) * mm});
            skLineSegment(sketch, "E168.right", {"start": v(-26.5, 2.5) * mm, "end": v(-26.5, 16) * mm});
            skLineSegment(sketch, "E169.trimOffspring", {"start": v(-26.5, 2.5) * mm, "end": v(-60, 2.5) * mm});
            skSolve(sketch);
        }
        {
            var Q0;
            Q0 = qSketchRegion(id + "F26", true);
            extrude(context, id + "F27", {"entities" : qUnion([Q0]), "operationType" : NewBodyOperationType.REMOVE, "depth" : 6 * mm});
        }
        {
            var Q0;
            Q0=makeQuery(id+"F13.boolean.opBoolean","MERGE",FACE,{"derivedFrom":[makeQuery(id+"F11.boolean.opBoolean","COPY",FACE,{"derivedFrom":makeQuery(id+"F11.opExtrude","CAP_FACE",FACE,{"disambiguationData":[OSD([sQuery(id+"F10.wireOp",EDGE,"E135.bottom"),sQuery(id+"F10.wireOp",EDGE,"E135.top"),sQuery(id+"F10.wireOp",EDGE,"E135.left"),sQuery(id+"F10.wireOp",EDGE,"E135.right"),sQuery(id+"F10.wireOp",EDGE,"E136.0"),sQuery(id+"F10.wireOp",EDGE,"E137.bottom"),sQuery(id+"F10.wireOp",EDGE,"E137.left"),sQuery(id+"F10.wireOp",EDGE,"E137.right")])],"isStart":false})}),makeQuery(id+"F13.opExtrude","CAP_FACE",FACE,{"disambiguationData":[OSD([sQuery(id+"F12.wireOp",EDGE,"E138.0"),sQuery(id+"F12.wireOp",EDGE,"E138.2"),sQuery(id+"F12.wireOp",EDGE,"E138.1"),sQuery(id+"F12.wireOp",EDGE,"E139"),sQuery(id+"F12.wireOp",EDGE,"E140"),sQuery(id+"F12.wireOp",EDGE,"E141.0"),sQuery(id+"F12.wireOp",EDGE,"E141.1"),sQuery(id+"F12.wireOp",EDGE,"E141.2")])],"isStart":true}),makeQuery(id+"F13.opExtrude","CAP_FACE",FACE,{"disambiguationData":[OSD([sQuery(id+"F12.wireOp",EDGE,"E142.1.0.4"),sQuery(id+"F12.wireOp",EDGE,"E142.1.0.5"),sQuery(id+"F12.wireOp",EDGE,"E142.1.0.6"),sQuery(id+"F12.wireOp",EDGE,"E142.1.0.7"),sQuery(id+"F12.wireOp",EDGE,"E142.1.0.8"),sQuery(id+"F12.wireOp",EDGE,"E142.1.0.9"),sQuery(id+"F12.wireOp",EDGE,"E142.1.0.10"),sQuery(id+"F12.wireOp",EDGE,"E142.1.0.11")])],"isStart":true}),makeQuery(id+"F13.opExtrude","CAP_FACE",FACE,{"disambiguationData":[OSD([sQuery(id+"F12.wireOp",EDGE,"E143"),sQuery(id+"F12.wireOp",EDGE,"E144")])],"isStart":true})]});
            var sketch = newSketch(context, id + "F28", { "sketchPlane" : qUnion([Q0])});
            skLineSegment(sketch, "E170.bottom", {"start": v(1.5, 17.67) * mm, "end": v(-1.5, 17.67) * mm});
            skLineSegment(sketch, "E170.top", {"start": v(1.5, 29.67) * mm, "end": v(-1.5, 29.67) * mm});
            skLineSegment(sketch, "E170.left", {"start": v(1.5, 17.67) * mm, "end": v(1.5, 29.67) * mm});
            skLineSegment(sketch, "E170.right", {"start": v(-1.5, 17.67) * mm, "end": v(-1.5, 29.67) * mm});
            skPoint(sketch, "E170.middle", {"position": v(0, 23.67) * mm});
            skSolve(sketch);
        }
        {
            var Q0;
            {var subQ0=makeQuery(id+"F11.boolean.opBoolean","INTERSECT",EDGE,{"derivedFrom":[makeQuery(id+"F1.opExtrude","SWEPT_FACE",FACE,{"disambiguationData":[OSD([sQuery(id+"F0.wireOp",EDGE,"E8")])]}),makeQuery(id+"F11.opExtrude","CAP_FACE",FACE,{"disambiguationData":[OSD([sQuery(id+"F10.wireOp",EDGE,"E135.bottom"),sQuery(id+"F10.wireOp",EDGE,"E135.top"),sQuery(id+"F10.wireOp",EDGE,"E135.left"),sQuery(id+"F10.wireOp",EDGE,"E135.right"),sQuery(id+"F10.wireOp",EDGE,"E136.0"),sQuery(id+"F10.wireOp",EDGE,"E137.bottom"),sQuery(id+"F10.wireOp",EDGE,"E137.left"),sQuery(id+"F10.wireOp",EDGE,"E137.right")])],"isStart":false})]});var subQ2=sQuery(id+"F28.wireOp",EDGE,"E170.left");var subQ3=makeQuery(id+"F28.imprint","INTERSECT",VERTEX,{"disambiguationData":[OD(0.0)],"derivedFrom":[subQ0,subQ2]});Q0=makeQuery(id+"F28.imprint","IMPRINT",FACE,{"disambiguationData":[TD([[makeQuery(id+"F28.imprint","IMPRINT",EDGE,{"disambiguationData":[TD([[subQ3,-1.0]])],"derivedFrom":subQ2}),1.0]])]});}
            extrude(context, id + "F29", {"entities" : qUnion([Q0]), "operationType" : NewBodyOperationType.ADD, "oppositeDirection" : true, "depth" : 2 * mm, "offsetDistance" : 25 * mm});
        }
        {
            var Q0;
            Q0=makeQuery(id+"F3.opExtrude","CAP_EDGE",EDGE,{"disambiguationData":[OSD([sQuery(id+"F2.wireOp",EDGE,"E41.right")])],"isStart":false});
            var Q1;
            Q1=makeQuery(id+"F3.opExtrude","CAP_EDGE",EDGE,{"disambiguationData":[OSD([sQuery(id+"F2.wireOp",EDGE,"E41.bottom")])],"isStart":false});
            var Q2;
            Q2=makeQuery(id+"F3.opExtrude","CAP_EDGE",EDGE,{"disambiguationData":[OSD([sQuery(id+"F2.wireOp",EDGE,"E41.left")])],"isStart":false});
            var Q3;
            Q3=makeQuery(id+"F3.opExtrude","CAP_EDGE",EDGE,{"disambiguationData":[OSD([sQuery(id+"F2.wireOp",EDGE,"E41.top")])],"isStart":false});
            var Q4;
            Q4=makeQuery(id+"F22.opExtrude","CAP_EDGE",EDGE,{"disambiguationData":[OSD([sQuery(id+"F21.wireOp",EDGE,"E165.right")])],"isStart":false});
            var Q5;
            Q5=makeQuery(id+"F22.opExtrude","CAP_EDGE",EDGE,{"disambiguationData":[OSD([sQuery(id+"F21.wireOp",EDGE,"E165.top")])],"isStart":false});
            var Q6;
            Q6=makeQuery(id+"F22.opExtrude","CAP_EDGE",EDGE,{"disambiguationData":[OSD([sQuery(id+"F21.wireOp",EDGE,"E165.left")])],"isStart":false});
            var Q7;
            Q7=makeQuery(id+"F22.opExtrude","CAP_EDGE",EDGE,{"disambiguationData":[OSD([sQuery(id+"F21.wireOp",EDGE,"E165.bottom")])],"isStart":false});
            fillet(context, id + "F30", {"entities" : qUnion([Q0, Q1, Q2, Q3, Q4, Q5, Q6, Q7]), "radius" : 0.5 * mm, "tangentPropagation" : true, "allowEdgeOverflow" : false});
        }
    });
